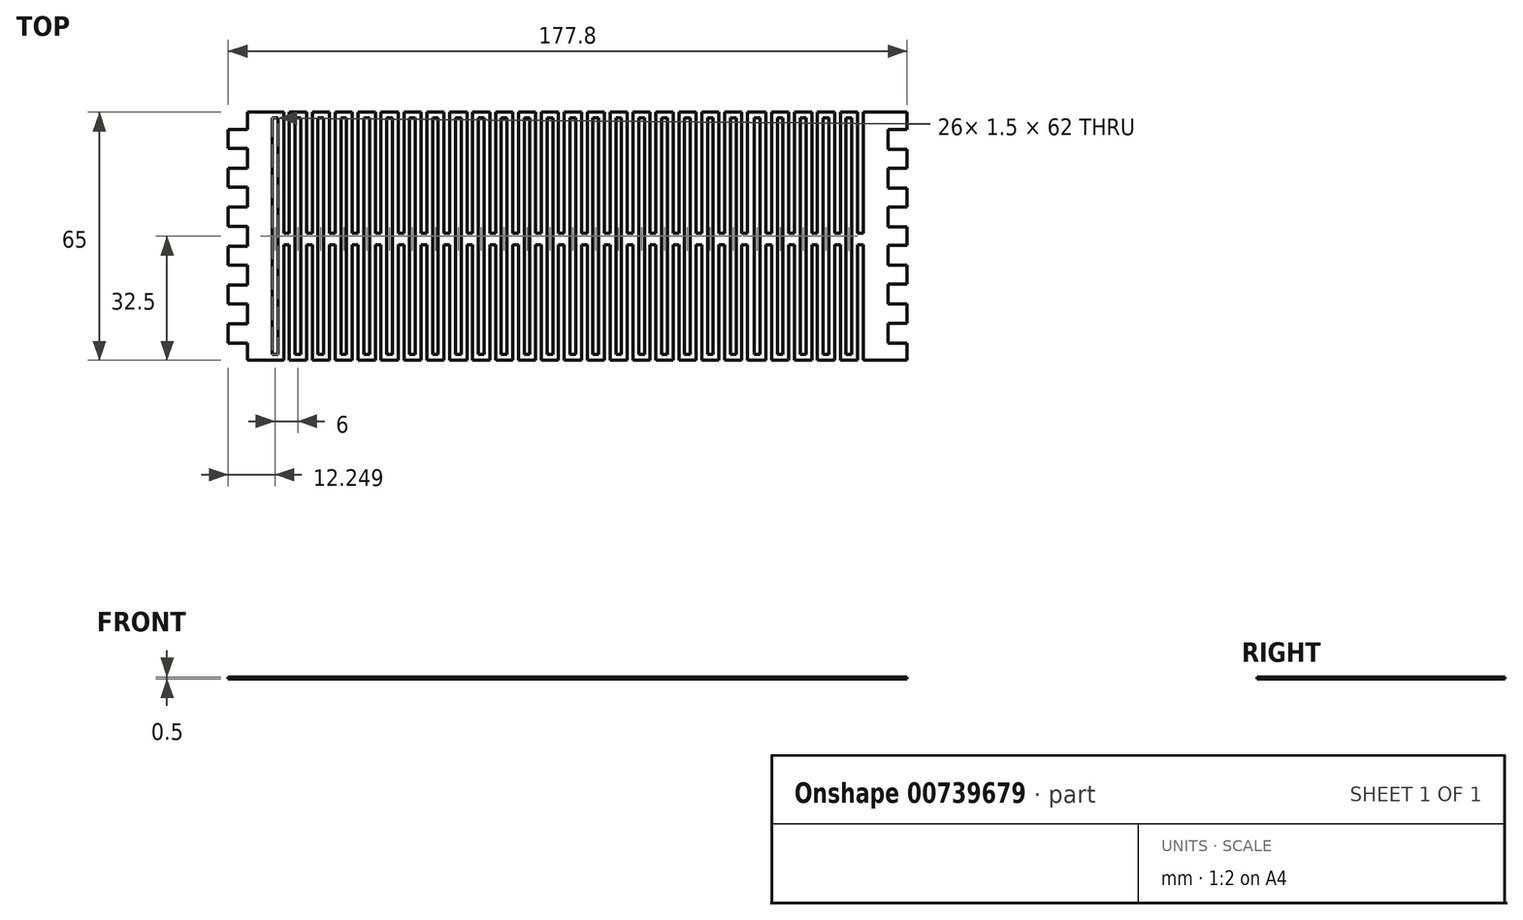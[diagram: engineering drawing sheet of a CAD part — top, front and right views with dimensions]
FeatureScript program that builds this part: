
annotation { "Feature Type Name" : "Feature", "Feature Type Description" : "" }
export const myFeature = defineFeature(function(context is Context, id is Id, definition is map)
    precondition{}
    {
        {
            var Q0;
            Q0=qCreatedBy(makeId("Top.planeOp"),FACE);
            var sketch = newSketch(context, id + "F0", { "sketchPlane" : qUnion([Q0])});
            skLineSegment(sketch, "E0.bottom", {"start": v(-70.46, 0) * mm, "end": v(-60.96, 0) * mm});
            skLineSegment(sketch, "E0.top", {"start": v(-70.46, -65) * mm, "end": v(-65.46, -65) * mm});
            skLineSegment(sketch, "E0.left", {"start": v(-75.46, -4.5) * mm, "end": v(-75.46, -9.5) * mm});
            skLineSegment(sketch, "E0.right", {"start": v(102.34, 0) * mm, "end": v(102.34, -4.5) * mm});
            skLineSegment(sketch, "E1.top", {"start": v(-75.46, -4.5) * mm, "end": v(-70.46, -4.5) * mm});
            skLineSegment(sketch, "E1.right", {"start": v(-70.46, 0) * mm, "end": v(-70.46, -4.5) * mm});
            skLineSegment(sketch, "E2", {"start": v(-70.46, -9.5) * mm, "end": v(-70.46, -14.7) * mm});
            skLineSegment(sketch, "E3", {"start": v(-65.46, 0) * mm, "end": v(-70.46, 0) * mm});
            skLineSegment(sketch, "E4", {"start": v(-75.46, -9.5) * mm, "end": v(-70.46, -9.5) * mm});
            skLineSegment(sketch, "E5", {"start": v(-70.46, -14.7) * mm, "end": v(-75.46, -14.7) * mm});
            skLineSegment(sketch, "E6", {"start": v(-75.46, -14.7) * mm, "end": v(-75.46, -19.7) * mm});
            skLineSegment(sketch, "E7", {"start": v(-75.46, -19.7) * mm, "end": v(-70.46, -19.7) * mm});
            skLineSegment(sketch, "E8", {"start": v(-70.46, -19.7) * mm, "end": v(-70.46, -24.9) * mm});
            skLineSegment(sketch, "E9", {"start": v(-70.46, -24.9) * mm, "end": v(-75.46, -24.9) * mm});
            skLineSegment(sketch, "E10", {"start": v(-75.46, -29.9) * mm, "end": v(-70.46, -29.9) * mm});
            skLineSegment(sketch, "E11", {"start": v(-70.46, -29.9) * mm, "end": v(-70.46, -35.1) * mm});
            skLineSegment(sketch, "E12", {"start": v(-70.46, -35.1) * mm, "end": v(-75.46, -35.1) * mm});
            skLineSegment(sketch, "E13", {"start": v(-75.46, -35.1) * mm, "end": v(-75.46, -40.1) * mm});
            skLineSegment(sketch, "E14", {"start": v(-75.46, -40.1) * mm, "end": v(-70.46, -40.1) * mm});
            skLineSegment(sketch, "E15", {"start": v(-70.46, -40.1) * mm, "end": v(-70.46, -45.3) * mm});
            skLineSegment(sketch, "E16", {"start": v(-70.46, -45.3) * mm, "end": v(-75.46, -45.3) * mm});
            skLineSegment(sketch, "E17", {"start": v(-75.46, -45.3) * mm, "end": v(-75.46, -50.3) * mm});
            skLineSegment(sketch, "E18", {"start": v(-75.46, -50.3) * mm, "end": v(-70.46, -50.3) * mm});
            skLineSegment(sketch, "E19", {"start": v(-70.46, -50.3) * mm, "end": v(-70.46, -55.5) * mm});
            skLineSegment(sketch, "E20", {"start": v(-70.46, -55.5) * mm, "end": v(-75.46, -55.5) * mm});
            skLineSegment(sketch, "E21", {"start": v(-75.46, -55.5) * mm, "end": v(-75.46, -60.5) * mm});
            skLineSegment(sketch, "E22", {"start": v(-75.46, -60.5) * mm, "end": v(-70.46, -60.5) * mm});
            skLineSegment(sketch, "E23", {"start": v(-70.46, -60.5) * mm, "end": v(-70.46, -65) * mm});
            skPoint(sketch, "E24.trimOffspring.end.orphan", {"position": v(-75.46, -65) * mm});
            skPoint(sketch, "E25.orphan", {"position": v(-75.46, 0) * mm});
            skPoint(sketch, "E26.start.orphan", {"position": v(-75.46, -28.38) * mm});
            skLineSegment(sketch, "E27", {"start": v(-75.46, -24.9) * mm, "end": v(-75.46, -29.9) * mm});
            skPoint(sketch, "E28.endSnap0", {"position": v(15.94, -65) * mm});
            skLineSegment(sketch, "E29.MirrorCS", {"start": v(92.34, 0) * mm, "end": v(97.34, 0) * mm});
            skPoint(sketch, "E30.MirrorCS.end.orphan", {"position": v(102.34, -10) * mm});
            skPoint(sketch, "E30.MirrorCS.start.orphan", {"position": v(102.34, -4.5) * mm});
            skPoint(sketch, "E31.MirrorCS.start.orphan", {"position": v(102.34, -34.9) * mm});
            skPoint(sketch, "E32.MirrorCS.end.orphan", {"position": v(102.34, -60.5) * mm});
            skPoint(sketch, "E32.MirrorCS.start.orphan", {"position": v(102.34, -55) * mm});
            skPoint(sketch, "E33.MirrorCS.end.orphan", {"position": v(97.34, -62.94) * mm});
            skPoint(sketch, "E34.MirrorCS.start.orphan", {"position": v(97.34, -50) * mm});
            skPoint(sketch, "E35.MirrorCS.start.orphan", {"position": v(97.34, -40.1) * mm});
            skPoint(sketch, "E36.MirrorCS.start.orphan", {"position": v(97.34, -30) * mm});
            skPoint(sketch, "E37.MirrorCS.end.orphan", {"position": v(97.34, -25) * mm});
            skPoint(sketch, "E37.MirrorCS.start.orphan", {"position": v(97.34, -20) * mm});
            skPoint(sketch, "E38.MirrorCS.start.orphan", {"position": v(97.34, -10) * mm});
            skPoint(sketch, "E39.MirrorCS.start.orphan", {"position": v(97.34, 0) * mm});
            skPoint(sketch, "E28.end.orphan", {"position": v(13.44, -65) * mm});
            skLineSegment(sketch, "E40", {"start": v(13.44, -65) * mm, "end": v(15.94, -65) * mm});
            skLineSegment(sketch, "E41", {"start": v(13.44, -65) * mm, "end": v(12.54, -65) * mm});
            skLineSegment(sketch, "E42", {"start": v(-70.46, -65) * mm, "end": v(-70.46, -60.5) * mm});
            skLineSegment(sketch, "E43", {"start": v(-70.46, -4.5) * mm, "end": v(-70.46, 0) * mm});
            skLineSegment(sketch, "E44", {"start": v(102.34, -9.7) * mm, "end": v(102.34, -14.7) * mm});
            skLineSegment(sketch, "E45", {"start": v(102.34, -65) * mm, "end": v(102.34, -60.5) * mm});
            skLineSegment(sketch, "E46", {"start": v(97.34, -4.5) * mm, "end": v(97.34, -9.7) * mm});
            skLineSegment(sketch, "E47", {"start": v(102.34, -60.5) * mm, "end": v(97.34, -60.5) * mm});
            skLineSegment(sketch, "E48", {"start": v(97.34, -60.5) * mm, "end": v(97.34, -55.3) * mm});
            skLineSegment(sketch, "E49", {"start": v(97.34, -55.3) * mm, "end": v(102.34, -55.3) * mm});
            skLineSegment(sketch, "E50", {"start": v(102.34, -55.3) * mm, "end": v(102.34, -50.3) * mm});
            skLineSegment(sketch, "E51", {"start": v(102.34, -50.3) * mm, "end": v(97.34, -50.3) * mm});
            skLineSegment(sketch, "E52", {"start": v(97.34, -50.3) * mm, "end": v(97.34, -45.1) * mm});
            skLineSegment(sketch, "E53", {"start": v(97.34, -45.1) * mm, "end": v(102.34, -45.1) * mm});
            skLineSegment(sketch, "E54", {"start": v(102.34, -45.1) * mm, "end": v(102.34, -40.1) * mm});
            skLineSegment(sketch, "E55", {"start": v(102.34, -40.1) * mm, "end": v(97.34, -40.1) * mm});
            skLineSegment(sketch, "E56", {"start": v(97.34, -40.1) * mm, "end": v(97.34, -34.9) * mm});
            skLineSegment(sketch, "E57.trimOffspring", {"start": v(102.34, -60.5) * mm, "end": v(102.34, -65) * mm});
            skLineSegment(sketch, "E58.trimOffspring", {"start": v(102.34, -50.3) * mm, "end": v(102.34, -55.3) * mm});
            skLineSegment(sketch, "E59.trimOffspring", {"start": v(102.34, -40.1) * mm, "end": v(102.34, -45.1) * mm});
            skLineSegment(sketch, "E60.trimOffspring", {"start": v(97.34, -55.3) * mm, "end": v(97.34, -60.5) * mm});
            skLineSegment(sketch, "E61.trimOffspring", {"start": v(97.34, -45.1) * mm, "end": v(97.34, -50.3) * mm});
            skLineSegment(sketch, "E62", {"start": v(102.34, -34.9) * mm, "end": v(97.34, -34.9) * mm});
            skLineSegment(sketch, "E63", {"start": v(97.34, -30.1) * mm, "end": v(102.34, -30.1) * mm});
            skLineSegment(sketch, "E64", {"start": v(102.34, -30.1) * mm, "end": v(102.34, -34.9) * mm});
            skLineSegment(sketch, "E65", {"start": v(97.34, -34.9) * mm, "end": v(97.34, -40.1) * mm});
            skLineSegment(sketch, "E66", {"start": v(97.34, -30.1) * mm, "end": v(97.34, -24.9) * mm});
            skLineSegment(sketch, "E67", {"start": v(97.34, -24.9) * mm, "end": v(102.34, -24.9) * mm});
            skLineSegment(sketch, "E68", {"start": v(102.34, -24.9) * mm, "end": v(102.34, -19.9) * mm});
            skLineSegment(sketch, "E69", {"start": v(102.34, -19.9) * mm, "end": v(97.34, -19.9) * mm});
            skLineSegment(sketch, "E70", {"start": v(97.34, -19.9) * mm, "end": v(97.34, -14.7) * mm});
            skLineSegment(sketch, "E71", {"start": v(97.34, -14.7) * mm, "end": v(102.34, -14.7) * mm});
            skLineSegment(sketch, "E72.trimOffspring", {"start": v(102.34, -19.9) * mm, "end": v(102.34, -24.9) * mm});
            skLineSegment(sketch, "E73.trimOffspring", {"start": v(97.34, -24.9) * mm, "end": v(97.34, -30.1) * mm});
            skLineSegment(sketch, "E74", {"start": v(97.34, -19.9) * mm, "end": v(102.34, -19.9) * mm});
            skLineSegment(sketch, "E75", {"start": v(102.34, -14.7) * mm, "end": v(102.34, -9.7) * mm});
            skLineSegment(sketch, "E76", {"start": v(102.34, -9.7) * mm, "end": v(97.34, -9.7) * mm});
            skLineSegment(sketch, "E77", {"start": v(97.34, -9.7) * mm, "end": v(97.34, -4.5) * mm});
            skLineSegment(sketch, "E78", {"start": v(97.34, -4.5) * mm, "end": v(102.34, -4.5) * mm});
            skLineSegment(sketch, "E79.trimOffspring", {"start": v(97.34, -14.7) * mm, "end": v(97.34, -19.9) * mm});
            skLineSegment(sketch, "E80.trimOffspring", {"start": v(13.44, -65) * mm, "end": v(17.04, -65) * mm});
            skLineSegment(sketch, "E81.bottom", {"start": v(-65.46, -65) * mm, "end": v(-63.96, -65) * mm});
            skLineSegment(sketch, "E82.bottom", {"start": v(-65.46, 0) * mm, "end": v(-63.96, 0) * mm});
            skLineSegment(sketch, "E83.bottom", {"start": v(-63.96, -1.5) * mm, "end": v(-62.46, -1.5) * mm});
            skLineSegment(sketch, "E83.top", {"start": v(-63.96, -63.5) * mm, "end": v(-62.46, -63.5) * mm});
            skLineSegment(sketch, "E83.left", {"start": v(-63.96, -1.5) * mm, "end": v(-63.96, -63.5) * mm});
            skLineSegment(sketch, "E83.right", {"start": v(-62.46, -1.5) * mm, "end": v(-62.46, -63.5) * mm});
            skPoint(sketch, "E81.top.end.orphan", {"position": v(-63.96, -63.5) * mm});
            skLineSegment(sketch, "E84.top", {"start": v(-62.46, -65) * mm, "end": v(-60.96, -65) * mm});
            skLineSegment(sketch, "E85.left", {"start": v(-60.96, -65) * mm, "end": v(-60.96, -34.75) * mm});
            skLineSegment(sketch, "E85.right", {"start": v(-59.46, -65) * mm, "end": v(-59.46, -34.75) * mm});
            skLineSegment(sketch, "E86.trimOffspring", {"start": v(-60.96, -65) * mm, "end": v(-70.46, -65) * mm});
            skLineSegment(sketch, "E87.top", {"start": v(-62.46, 0) * mm, "end": v(-60.96, 0) * mm});
            skLineSegment(sketch, "E87.right", {"start": v(-60.96, -1.5) * mm, "end": v(-60.96, 0) * mm});
            skLineSegment(sketch, "E88.top", {"start": v(-60.96, -31.75) * mm, "end": v(-59.46, -31.75) * mm});
            skLineSegment(sketch, "E88.left", {"start": v(-60.96, -1.5) * mm, "end": v(-60.96, -31.75) * mm});
            skLineSegment(sketch, "E88.right", {"start": v(-59.46, -1.5) * mm, "end": v(-59.46, -31.75) * mm});
            skLineSegment(sketch, "E89.trimOffspring", {"start": v(13.44, 0) * mm, "end": v(17.04, 0) * mm});
            skLineSegment(sketch, "E90", {"start": v(-59.46, -1.5) * mm, "end": v(-59.46, 0) * mm});
            skLineSegment(sketch, "E91.trimOffspring", {"start": v(-59.46, 0) * mm, "end": v(-54.96, 0) * mm});
            skLineSegment(sketch, "E92.bottom", {"start": v(-59.46, -65) * mm, "end": v(-57.96, -65) * mm});
            skLineSegment(sketch, "E92.left", {"start": v(-59.46, -65) * mm, "end": v(-59.46, -63.5) * mm});
            skLineSegment(sketch, "E93.bottom", {"start": v(-59.46, 0) * mm, "end": v(-57.96, 0) * mm});
            skLineSegment(sketch, "E93.left", {"start": v(-59.46, 0) * mm, "end": v(-59.46, -1.5) * mm});
            skLineSegment(sketch, "E94.bottom", {"start": v(-57.96, -1.5) * mm, "end": v(-56.46, -1.5) * mm});
            skLineSegment(sketch, "E94.top", {"start": v(-57.96, -63.5) * mm, "end": v(-56.46, -63.5) * mm});
            skLineSegment(sketch, "E94.left", {"start": v(-57.96, -1.5) * mm, "end": v(-57.96, -63.5) * mm});
            skLineSegment(sketch, "E94.right", {"start": v(-56.46, -1.5) * mm, "end": v(-56.46, -63.5) * mm});
            skLineSegment(sketch, "E95.trimOffspring", {"start": v(-59.46, -31.75) * mm, "end": v(-60.96, -31.75) * mm});
            skLineSegment(sketch, "E96.top", {"start": v(-56.46, -65) * mm, "end": v(-54.96, -65) * mm});
            skLineSegment(sketch, "E97.bottom", {"start": v(-56.46, -1.5) * mm, "end": v(-54.96, -1.5) * mm});
            skLineSegment(sketch, "E97.top", {"start": v(-56.46, 0) * mm, "end": v(-54.96, 0) * mm});
            skLineSegment(sketch, "E98.top", {"start": v(-54.96, -31.75) * mm, "end": v(-53.46, -31.75) * mm});
            skLineSegment(sketch, "E98.left", {"start": v(-54.96, -1.5) * mm, "end": v(-54.96, -31.75) * mm});
            skLineSegment(sketch, "E98.right", {"start": v(-53.46, -1.5) * mm, "end": v(-53.46, -31.75) * mm});
            skLineSegment(sketch, "E99", {"start": v(-54.96, -1.5) * mm, "end": v(-54.96, 0) * mm});
            skLineSegment(sketch, "E100", {"start": v(-53.46, -1.5) * mm, "end": v(-53.46, 0) * mm});
            skLineSegment(sketch, "E101.trimOffspring", {"start": v(-53.46, 0) * mm, "end": v(-48.96, 0) * mm});
            skPoint(sketch, "E96.right.start.orphan", {"position": v(-54.96, -63.5) * mm});
            skLineSegment(sketch, "E102.left", {"start": v(-54.96, -65) * mm, "end": v(-54.96, -34.75) * mm});
            skLineSegment(sketch, "E102.right", {"start": v(-53.46, -65) * mm, "end": v(-53.46, -34.75) * mm});
            skLineSegment(sketch, "E103.trimOffspring", {"start": v(-54.96, -65) * mm, "end": v(-59.46, -65) * mm});
            skLineSegment(sketch, "E104.bottom", {"start": v(-53.46, -65) * mm, "end": v(-51.96, -65) * mm});
            skLineSegment(sketch, "E104.left", {"start": v(-53.46, -65) * mm, "end": v(-53.46, -63.5) * mm});
            skLineSegment(sketch, "E105.bottom", {"start": v(-53.46, 0) * mm, "end": v(-51.96, 0) * mm});
            skLineSegment(sketch, "E105.left", {"start": v(-53.46, 0) * mm, "end": v(-53.46, -1.5) * mm});
            skLineSegment(sketch, "E106.bottom", {"start": v(-51.96, -1.5) * mm, "end": v(-50.46, -1.5) * mm});
            skLineSegment(sketch, "E106.top", {"start": v(-51.96, -63.5) * mm, "end": v(-50.46, -63.5) * mm});
            skLineSegment(sketch, "E106.left", {"start": v(-51.96, -1.5) * mm, "end": v(-51.96, -63.5) * mm});
            skLineSegment(sketch, "E106.right", {"start": v(-50.46, -1.5) * mm, "end": v(-50.46, -63.5) * mm});
            skLineSegment(sketch, "E107.trimOffspring", {"start": v(-53.46, -31.75) * mm, "end": v(-54.96, -31.75) * mm});
            skLineSegment(sketch, "E108.top", {"start": v(-50.46, -65) * mm, "end": v(-48.96, -65) * mm});
            skLineSegment(sketch, "E108.right", {"start": v(-48.96, -63.5) * mm, "end": v(-48.96, -65) * mm});
            skLineSegment(sketch, "E109.left", {"start": v(-48.96, -65) * mm, "end": v(-48.96, -34.75) * mm});
            skLineSegment(sketch, "E109.right", {"start": v(-47.46, -65) * mm, "end": v(-47.46, -34.75) * mm});
            skLineSegment(sketch, "E110.trimOffspring", {"start": v(-48.96, -65) * mm, "end": v(-53.46, -65) * mm});
            skLineSegment(sketch, "E111.top", {"start": v(-50.46, 0) * mm, "end": v(-48.96, 0) * mm});
            skLineSegment(sketch, "E111.right", {"start": v(-48.96, -1.5) * mm, "end": v(-48.96, 0) * mm});
            skLineSegment(sketch, "E112.top", {"start": v(-48.96, -31.75) * mm, "end": v(-47.46, -31.75) * mm});
            skLineSegment(sketch, "E112.left", {"start": v(-48.96, -1.5) * mm, "end": v(-48.96, -31.75) * mm});
            skLineSegment(sketch, "E112.right", {"start": v(-47.46, -1.5) * mm, "end": v(-47.46, -31.75) * mm});
            skLineSegment(sketch, "E113", {"start": v(-47.46, -1.5) * mm, "end": v(-47.46, 0) * mm});
            skLineSegment(sketch, "E114.trimOffspring", {"start": v(-47.46, 0) * mm, "end": v(-42.96, 0) * mm});
            skLineSegment(sketch, "E115.bottom", {"start": v(-47.46, -65) * mm, "end": v(-45.96, -65) * mm});
            skLineSegment(sketch, "E115.left", {"start": v(-47.46, -65) * mm, "end": v(-47.46, -63.5) * mm});
            skLineSegment(sketch, "E116.bottom", {"start": v(-47.46, 0) * mm, "end": v(-45.96, 0) * mm});
            skLineSegment(sketch, "E116.left", {"start": v(-47.46, 0) * mm, "end": v(-47.46, -1.5) * mm});
            skLineSegment(sketch, "E117.bottom", {"start": v(-45.96, -1.5) * mm, "end": v(-44.46, -1.5) * mm});
            skLineSegment(sketch, "E117.top", {"start": v(-45.96, -63.5) * mm, "end": v(-44.46, -63.5) * mm});
            skLineSegment(sketch, "E117.left", {"start": v(-45.96, -1.5) * mm, "end": v(-45.96, -63.5) * mm});
            skLineSegment(sketch, "E117.right", {"start": v(-44.46, -1.5) * mm, "end": v(-44.46, -63.5) * mm});
            skLineSegment(sketch, "E118.trimOffspring", {"start": v(-47.46, -31.75) * mm, "end": v(-48.96, -31.75) * mm});
            skLineSegment(sketch, "E119.top", {"start": v(-44.46, -65) * mm, "end": v(-42.96, -65) * mm});
            skLineSegment(sketch, "E119.right", {"start": v(-42.96, -63.5) * mm, "end": v(-42.96, -65) * mm});
            skLineSegment(sketch, "E120.left", {"start": v(-42.96, -65) * mm, "end": v(-42.96, -34.75) * mm});
            skLineSegment(sketch, "E120.right", {"start": v(-41.46, -65) * mm, "end": v(-41.46, -34.75) * mm});
            skLineSegment(sketch, "E121.trimOffspring", {"start": v(-42.96, -65) * mm, "end": v(-47.46, -65) * mm});
            skLineSegment(sketch, "E122.top", {"start": v(-44.46, 0) * mm, "end": v(-42.96, 0) * mm});
            skLineSegment(sketch, "E122.right", {"start": v(-42.96, -1.5) * mm, "end": v(-42.96, 0) * mm});
            skLineSegment(sketch, "E123.top", {"start": v(-42.96, -31.75) * mm, "end": v(-41.46, -31.75) * mm});
            skLineSegment(sketch, "E123.left", {"start": v(-42.96, 0) * mm, "end": v(-42.96, -31.75) * mm});
            skLineSegment(sketch, "E123.right", {"start": v(-41.46, 0) * mm, "end": v(-41.46, -31.75) * mm});
            skLineSegment(sketch, "E124.trimOffspring", {"start": v(-41.46, 0) * mm, "end": v(-36.96, 0) * mm});
            skLineSegment(sketch, "E125.bottom", {"start": v(-41.46, -65) * mm, "end": v(-39.96, -65) * mm});
            skLineSegment(sketch, "E125.left", {"start": v(-41.46, -65) * mm, "end": v(-41.46, -63.5) * mm});
            skLineSegment(sketch, "E126.bottom", {"start": v(-41.46, 0) * mm, "end": v(-39.96, 0) * mm});
            skLineSegment(sketch, "E126.left", {"start": v(-41.46, 0) * mm, "end": v(-41.46, -1.5) * mm});
            skLineSegment(sketch, "E127.bottom", {"start": v(-39.96, -1.5) * mm, "end": v(-38.46, -1.5) * mm});
            skLineSegment(sketch, "E127.top", {"start": v(-39.96, -63.5) * mm, "end": v(-38.46, -63.5) * mm});
            skLineSegment(sketch, "E127.left", {"start": v(-39.96, -1.5) * mm, "end": v(-39.96, -63.5) * mm});
            skLineSegment(sketch, "E127.right", {"start": v(-38.46, -1.5) * mm, "end": v(-38.46, -63.5) * mm});
            skPoint(sketch, "E125.right.end.orphan", {"position": v(-39.96, -63.5) * mm});
            skLineSegment(sketch, "E128.trimOffspring", {"start": v(-41.46, -31.75) * mm, "end": v(-42.96, -31.75) * mm});
            skLineSegment(sketch, "E129.top", {"start": v(-38.46, -65) * mm, "end": v(-36.96, -65) * mm});
            skLineSegment(sketch, "E130.top", {"start": v(-38.46, 0) * mm, "end": v(-36.96, 0) * mm});
            skLineSegment(sketch, "E130.right", {"start": v(-36.96, -1.5) * mm, "end": v(-36.96, 0) * mm});
            skLineSegment(sketch, "E131.top", {"start": v(-36.96, -31.75) * mm, "end": v(-35.46, -31.75) * mm});
            skLineSegment(sketch, "E131.left", {"start": v(-36.96, -1.5) * mm, "end": v(-36.96, -31.75) * mm});
            skLineSegment(sketch, "E131.right", {"start": v(-35.46, -1.5) * mm, "end": v(-35.46, -31.75) * mm});
            skLineSegment(sketch, "E132", {"start": v(-35.46, -1.5) * mm, "end": v(-35.46, 0) * mm});
            skLineSegment(sketch, "E133.trimOffspring", {"start": v(-35.46, 0) * mm, "end": v(-32.46, 0) * mm});
            skLineSegment(sketch, "E134.right", {"start": v(-36.96, -65) * mm, "end": v(-36.96, -63.5) * mm});
            skLineSegment(sketch, "E135.top", {"start": v(-36.96, -34.75) * mm, "end": v(-35.46, -34.75) * mm});
            skLineSegment(sketch, "E135.left", {"start": v(-36.96, -65) * mm, "end": v(-36.96, -34.75) * mm});
            skLineSegment(sketch, "E135.right", {"start": v(-35.46, -65) * mm, "end": v(-35.46, -34.75) * mm});
            skLineSegment(sketch, "E136.trimOffspring", {"start": v(-38.46, -65) * mm, "end": v(-41.46, -65) * mm});
            skLineSegment(sketch, "E137.bottom", {"start": v(-35.46, -65) * mm, "end": v(-33.96, -65) * mm});
            skLineSegment(sketch, "E137.left", {"start": v(-35.46, -65) * mm, "end": v(-35.46, -63.5) * mm});
            skLineSegment(sketch, "E138.bottom", {"start": v(-35.46, 0) * mm, "end": v(-33.96, 0) * mm});
            skLineSegment(sketch, "E138.left", {"start": v(-35.46, 0) * mm, "end": v(-35.46, -1.5) * mm});
            skLineSegment(sketch, "E139.bottom", {"start": v(-33.96, -1.5) * mm, "end": v(-32.46, -1.5) * mm});
            skLineSegment(sketch, "E139.top", {"start": v(-33.96, -63.5) * mm, "end": v(-32.46, -63.5) * mm});
            skLineSegment(sketch, "E139.left", {"start": v(-33.96, -1.5) * mm, "end": v(-33.96, -63.5) * mm});
            skLineSegment(sketch, "E139.right", {"start": v(-32.46, -1.5) * mm, "end": v(-32.46, -63.5) * mm});
            skPoint(sketch, "E137.top.end.orphan", {"position": v(-33.96, -63.5) * mm});
            skLineSegment(sketch, "E140.trimOffspring", {"start": v(-35.46, -31.75) * mm, "end": v(-36.96, -31.75) * mm});
            skLineSegment(sketch, "E141.trimOffspring", {"start": v(-59.46, -34.75) * mm, "end": v(-60.96, -34.75) * mm});
            skLineSegment(sketch, "E142.trimOffspring", {"start": v(-53.46, -34.75) * mm, "end": v(-54.96, -34.75) * mm});
            skLineSegment(sketch, "E143.trimOffspring", {"start": v(-47.46, -34.75) * mm, "end": v(-48.96, -34.75) * mm});
            skLineSegment(sketch, "E144.trimOffspring", {"start": v(-41.46, -34.75) * mm, "end": v(-42.96, -34.75) * mm});
            skLineSegment(sketch, "E145.trimOffspring", {"start": v(-35.46, -34.75) * mm, "end": v(-36.96, -34.75) * mm});
            skLineSegment(sketch, "E146.MirrorCS", {"start": v(62.34, -1.5) * mm, "end": v(62.34, -31.75) * mm});
            skLineSegment(sketch, "E147.MirrorCS", {"start": v(63.84, -1.5) * mm, "end": v(63.84, -31.75) * mm});
            skLineSegment(sketch, "E148.MirrorCS", {"start": v(65.34, -1.5) * mm, "end": v(65.34, -31.75) * mm});
            skLineSegment(sketch, "E149.MirrorCS", {"start": v(68.34, -1.5) * mm, "end": v(68.34, -31.75) * mm});
            skLineSegment(sketch, "E150.MirrorCS", {"start": v(69.84, -1.5) * mm, "end": v(69.84, -31.75) * mm});
            skLineSegment(sketch, "E151.MirrorCS", {"start": v(90.84, -1.5) * mm, "end": v(90.84, -31.75) * mm});
            skLineSegment(sketch, "E152.MirrorCS", {"start": v(89.34, -1.5) * mm, "end": v(89.34, -31.75) * mm});
            skLineSegment(sketch, "E153.MirrorCS", {"start": v(87.84, -1.5) * mm, "end": v(87.84, -31.75) * mm});
            skLineSegment(sketch, "E154.MirrorCS", {"start": v(86.34, -1.5) * mm, "end": v(86.34, -31.75) * mm});
            skLineSegment(sketch, "E155.MirrorCS", {"start": v(84.84, -1.5) * mm, "end": v(84.84, -31.75) * mm});
            skLineSegment(sketch, "E156.MirrorCS", {"start": v(81.84, -1.5) * mm, "end": v(81.84, -31.75) * mm});
            skLineSegment(sketch, "E157.MirrorCS", {"start": v(80.34, -1.5) * mm, "end": v(80.34, -31.75) * mm});
            skLineSegment(sketch, "E158.MirrorCS", {"start": v(78.84, -1.5) * mm, "end": v(78.84, -31.75) * mm});
            skLineSegment(sketch, "E159.MirrorCS", {"start": v(77.34, -1.5) * mm, "end": v(77.34, -31.75) * mm});
            skLineSegment(sketch, "E160.MirrorCS", {"start": v(75.84, -1.5) * mm, "end": v(75.84, -31.75) * mm});
            skLineSegment(sketch, "E161.MirrorCS", {"start": v(74.34, -1.5) * mm, "end": v(74.34, -31.75) * mm});
            skLineSegment(sketch, "E162.MirrorCS", {"start": v(72.84, -1.5) * mm, "end": v(72.84, -31.75) * mm});
            skLineSegment(sketch, "E163.MirrorCS", {"start": v(71.34, -1.5) * mm, "end": v(71.34, -31.75) * mm});
            skLineSegment(sketch, "E164.MirrorCS", {"start": v(62.34, -63.5) * mm, "end": v(62.34, -34.75) * mm});
            skLineSegment(sketch, "E165.MirrorCS", {"start": v(63.84, -63.5) * mm, "end": v(63.84, -34.75) * mm});
            skLineSegment(sketch, "E166.MirrorCS", {"start": v(68.34, -63.5) * mm, "end": v(68.34, -34.75) * mm});
            skLineSegment(sketch, "E167.MirrorCS", {"start": v(69.84, -63.5) * mm, "end": v(69.84, -34.75) * mm});
            skLineSegment(sketch, "E168.MirrorCS", {"start": v(75.84, -63.5) * mm, "end": v(75.84, -34.75) * mm});
            skLineSegment(sketch, "E169.MirrorCS", {"start": v(80.34, -63.5) * mm, "end": v(80.34, -34.75) * mm});
            skLineSegment(sketch, "E170.MirrorCS", {"start": v(81.84, -63.5) * mm, "end": v(81.84, -34.75) * mm});
            skLineSegment(sketch, "E171.MirrorCS", {"start": v(87.84, -63.5) * mm, "end": v(87.84, -34.75) * mm});
            skLineSegment(sketch, "E172.MirrorCS", {"start": v(66.84, -1.5) * mm, "end": v(66.84, -31.75) * mm});
            skLineSegment(sketch, "E173.MirrorCS", {"start": v(74.34, -63.5) * mm, "end": v(74.34, -34.75) * mm});
            skLineSegment(sketch, "E174.MirrorCS", {"start": v(86.34, -63.5) * mm, "end": v(86.34, -34.75) * mm});
            skLineSegment(sketch, "E175.MirrorCS", {"start": v(83.34, -1.5) * mm, "end": v(83.34, -31.75) * mm});
            skLineSegment(sketch, "E176.trimOffspring", {"start": v(63.84, -65) * mm, "end": v(65.34, -65) * mm});
            skLineSegment(sketch, "E177.trimOffspring", {"start": v(69.84, -65) * mm, "end": v(71.34, -65) * mm});
            skLineSegment(sketch, "E178.trimOffspring", {"start": v(75.84, -65) * mm, "end": v(77.34, -65) * mm});
            skLineSegment(sketch, "E179.trimOffspring", {"start": v(81.84, -65) * mm, "end": v(83.34, -65) * mm});
            skLineSegment(sketch, "E180.trimOffspring", {"start": v(87.84, -65) * mm, "end": v(89.34, -65) * mm});
            skLineSegment(sketch, "E181.trimOffspring", {"start": v(63.84, 0) * mm, "end": v(65.34, 0) * mm});
            skLineSegment(sketch, "E182.trimOffspring", {"start": v(69.84, 0) * mm, "end": v(71.34, 0) * mm});
            skLineSegment(sketch, "E183.trimOffspring", {"start": v(81.84, 0) * mm, "end": v(83.34, 0) * mm});
            skLineSegment(sketch, "E184.trimOffspring", {"start": v(87.84, 0) * mm, "end": v(89.34, 0) * mm});
            skLineSegment(sketch, "E185.trimOffspring", {"start": v(-36.96, -65) * mm, "end": v(-41.46, -65) * mm});
            skLineSegment(sketch, "E186.trimOffspring", {"start": v(-42.96, -65) * mm, "end": v(-45.96, -65) * mm});
            skLineSegment(sketch, "E187.trimOffspring", {"start": v(-48.96, -65) * mm, "end": v(-51.96, -65) * mm});
            skLineSegment(sketch, "E188.trimOffspring", {"start": v(-60.96, -65) * mm, "end": v(-75.46, -65) * mm});
            skLineSegment(sketch, "E189.top", {"start": v(-32.46, -65) * mm, "end": v(-30.96, -65) * mm});
            skLineSegment(sketch, "E189.right", {"start": v(-30.96, -63.5) * mm, "end": v(-30.96, -65) * mm});
            skLineSegment(sketch, "E190.top", {"start": v(-32.46, 0) * mm, "end": v(-30.96, 0) * mm});
            skLineSegment(sketch, "E190.right", {"start": v(-30.96, -1.5) * mm, "end": v(-30.96, 0) * mm});
            skLineSegment(sketch, "E191.top", {"start": v(-30.96, -34.75) * mm, "end": v(-29.46, -34.75) * mm});
            skLineSegment(sketch, "E191.left", {"start": v(-30.96, -63.5) * mm, "end": v(-30.96, -34.75) * mm});
            skLineSegment(sketch, "E191.right", {"start": v(-29.46, -63.5) * mm, "end": v(-29.46, -34.75) * mm});
            skLineSegment(sketch, "E192.top", {"start": v(-30.96, -31.75) * mm, "end": v(-29.46, -31.75) * mm});
            skLineSegment(sketch, "E192.left", {"start": v(-30.96, -1.5) * mm, "end": v(-30.96, -31.75) * mm});
            skLineSegment(sketch, "E192.right", {"start": v(-29.46, -1.5) * mm, "end": v(-29.46, -31.75) * mm});
            skLineSegment(sketch, "E193", {"start": v(-29.46, -63.5) * mm, "end": v(-29.46, -65) * mm});
            skLineSegment(sketch, "E194", {"start": v(-29.46, -65) * mm, "end": v(-29.46, -34.75) * mm});
            skLineSegment(sketch, "E195", {"start": v(-29.46, -1.5) * mm, "end": v(-29.46, 0) * mm});
            skLineSegment(sketch, "E196.trimOffspring", {"start": v(-29.46, 0) * mm, "end": v(-26.46, 0) * mm});
            skLineSegment(sketch, "E197.trimOffspring", {"start": v(-30.96, -65) * mm, "end": v(-35.46, -65) * mm});
            skLineSegment(sketch, "E198.trimOffspring", {"start": v(-30.96, -65) * mm, "end": v(-33.96, -65) * mm});
            skLineSegment(sketch, "E199.trimOffspring", {"start": v(-29.46, -31.75) * mm, "end": v(-29.46, -1.5) * mm});
            skLineSegment(sketch, "E200.bottom", {"start": v(-29.46, -65) * mm, "end": v(-27.96, -65) * mm});
            skLineSegment(sketch, "E200.left", {"start": v(-29.46, -65) * mm, "end": v(-29.46, -63.5) * mm});
            skLineSegment(sketch, "E201.bottom", {"start": v(-29.46, 0) * mm, "end": v(-27.96, 0) * mm});
            skLineSegment(sketch, "E201.left", {"start": v(-29.46, 0) * mm, "end": v(-29.46, -1.5) * mm});
            skLineSegment(sketch, "E202.bottom", {"start": v(-27.96, -1.5) * mm, "end": v(-26.46, -1.5) * mm});
            skLineSegment(sketch, "E202.top", {"start": v(-27.96, -63.5) * mm, "end": v(-26.46, -63.5) * mm});
            skLineSegment(sketch, "E202.left", {"start": v(-27.96, -1.5) * mm, "end": v(-27.96, -63.5) * mm});
            skLineSegment(sketch, "E202.right", {"start": v(-26.46, -1.5) * mm, "end": v(-26.46, -63.5) * mm});
            skLineSegment(sketch, "E203.trimOffspring", {"start": v(-29.46, -34.75) * mm, "end": v(-30.96, -34.75) * mm});
            skLineSegment(sketch, "E204.trimOffspring", {"start": v(-29.46, -31.75) * mm, "end": v(-30.96, -31.75) * mm});
            skLineSegment(sketch, "E205.top", {"start": v(-26.46, -65) * mm, "end": v(-24.96, -65) * mm});
            skLineSegment(sketch, "E205.right", {"start": v(-24.96, -63.5) * mm, "end": v(-24.96, -65) * mm});
            skLineSegment(sketch, "E206.top", {"start": v(-26.46, 0) * mm, "end": v(-24.96, 0) * mm});
            skLineSegment(sketch, "E206.right", {"start": v(-24.96, -1.5) * mm, "end": v(-24.96, 0) * mm});
            skLineSegment(sketch, "E207.top", {"start": v(-24.96, -31.75) * mm, "end": v(-23.46, -31.75) * mm});
            skLineSegment(sketch, "E207.left", {"start": v(-24.96, 0) * mm, "end": v(-24.96, -31.75) * mm});
            skLineSegment(sketch, "E207.right", {"start": v(-23.46, 0) * mm, "end": v(-23.46, -31.75) * mm});
            skLineSegment(sketch, "E208.top", {"start": v(-24.96, -34.75) * mm, "end": v(-23.46, -34.75) * mm});
            skLineSegment(sketch, "E208.left", {"start": v(-24.96, -65) * mm, "end": v(-24.96, -34.75) * mm});
            skLineSegment(sketch, "E208.right", {"start": v(-23.46, -65) * mm, "end": v(-23.46, -34.75) * mm});
            skLineSegment(sketch, "E209.trimOffspring", {"start": v(-24.96, -65) * mm, "end": v(-29.46, -65) * mm});
            skLineSegment(sketch, "E210.trimOffspring", {"start": v(-23.46, 0) * mm, "end": v(-18.96, 0) * mm});
            skLineSegment(sketch, "E211.bottom", {"start": v(-23.46, -65) * mm, "end": v(-21.96, -65) * mm});
            skLineSegment(sketch, "E211.left", {"start": v(-23.46, -65) * mm, "end": v(-23.46, -63.5) * mm});
            skLineSegment(sketch, "E212.bottom", {"start": v(-23.46, 0) * mm, "end": v(-21.96, 0) * mm});
            skLineSegment(sketch, "E212.left", {"start": v(-23.46, 0) * mm, "end": v(-23.46, -1.5) * mm});
            skLineSegment(sketch, "E213.bottom", {"start": v(-21.96, -1.5) * mm, "end": v(-20.46, -1.5) * mm});
            skLineSegment(sketch, "E213.top", {"start": v(-21.96, -63.5) * mm, "end": v(-20.46, -63.5) * mm});
            skLineSegment(sketch, "E213.left", {"start": v(-21.96, -1.5) * mm, "end": v(-21.96, -63.5) * mm});
            skLineSegment(sketch, "E213.right", {"start": v(-20.46, -1.5) * mm, "end": v(-20.46, -63.5) * mm});
            skPoint(sketch, "E211.right.end.orphan", {"position": v(-21.96, -63.5) * mm});
            skLineSegment(sketch, "E214.top", {"start": v(-20.46, -65) * mm, "end": v(-18.96, -65) * mm});
            skLineSegment(sketch, "E214.right", {"start": v(-18.96, -63.5) * mm, "end": v(-18.96, -65) * mm});
            skLineSegment(sketch, "E215.top", {"start": v(-20.46, 0) * mm, "end": v(-18.96, 0) * mm});
            skLineSegment(sketch, "E215.right", {"start": v(-18.96, -1.5) * mm, "end": v(-18.96, 0) * mm});
            skLineSegment(sketch, "E216.top", {"start": v(-18.96, -31.75) * mm, "end": v(-17.46, -31.75) * mm});
            skLineSegment(sketch, "E216.left", {"start": v(-18.96, 0) * mm, "end": v(-18.96, -31.75) * mm});
            skLineSegment(sketch, "E216.right", {"start": v(-17.46, 0) * mm, "end": v(-17.46, -31.75) * mm});
            skLineSegment(sketch, "E217.top", {"start": v(-18.96, -34.75) * mm, "end": v(-17.46, -34.75) * mm});
            skLineSegment(sketch, "E217.left", {"start": v(-18.96, -63.5) * mm, "end": v(-18.96, -34.75) * mm});
            skLineSegment(sketch, "E217.right", {"start": v(-17.46, -63.5) * mm, "end": v(-17.46, -34.75) * mm});
            skLineSegment(sketch, "E218", {"start": v(-17.46, -63.5) * mm, "end": v(-17.46, -65) * mm});
            skLineSegment(sketch, "E219.trimOffspring", {"start": v(-18.96, -65) * mm, "end": v(-23.46, -65) * mm});
            skLineSegment(sketch, "E220.trimOffspring", {"start": v(-17.46, 0) * mm, "end": v(-14.46, 0) * mm});
            skLineSegment(sketch, "E221.bottom", {"start": v(-17.46, -65) * mm, "end": v(-15.96, -65) * mm});
            skLineSegment(sketch, "E221.left", {"start": v(-17.46, -65) * mm, "end": v(-17.46, -63.5) * mm});
            skLineSegment(sketch, "E222.bottom", {"start": v(-17.46, 0) * mm, "end": v(-15.96, 0) * mm});
            skLineSegment(sketch, "E222.left", {"start": v(-17.46, 0) * mm, "end": v(-17.46, -1.5) * mm});
            skLineSegment(sketch, "E223.bottom", {"start": v(-15.96, 0) * mm, "end": v(-14.46, 0) * mm});
            skLineSegment(sketch, "E224.bottom", {"start": v(-15.96, -65) * mm, "end": v(-14.46, -65) * mm});
            skLineSegment(sketch, "E225.trimOffspring", {"start": v(-15.96, -65) * mm, "end": v(-17.46, -65) * mm});
            skLineSegment(sketch, "E226.bottom", {"start": v(-15.96, -63.5) * mm, "end": v(-14.46, -63.5) * mm});
            skLineSegment(sketch, "E226.left", {"start": v(-15.96, -63.5) * mm, "end": v(-15.96, -34.75) * mm});
            skLineSegment(sketch, "E226.right", {"start": v(-14.46, -63.5) * mm, "end": v(-14.46, -34.75) * mm});
            skLineSegment(sketch, "E227.left", {"start": v(-15.96, -34.75) * mm, "end": v(-15.96, -3) * mm});
            skLineSegment(sketch, "E227.right", {"start": v(-14.46, -34.75) * mm, "end": v(-14.46, -3) * mm});
            skLineSegment(sketch, "E228.bottom", {"start": v(-15.96, -1.5) * mm, "end": v(-14.46, -1.5) * mm});
            skLineSegment(sketch, "E228.left", {"start": v(-15.96, -1.5) * mm, "end": v(-15.96, -3) * mm});
            skLineSegment(sketch, "E228.right", {"start": v(-14.46, -1.5) * mm, "end": v(-14.46, -3) * mm});
            skLineSegment(sketch, "E229.top", {"start": v(-14.46, -65) * mm, "end": v(-12.96, -65) * mm});
            skLineSegment(sketch, "E229.right", {"start": v(-12.96, -63.5) * mm, "end": v(-12.96, -65) * mm});
            skLineSegment(sketch, "E230.top", {"start": v(-14.46, 0) * mm, "end": v(-12.96, 0) * mm});
            skLineSegment(sketch, "E230.right", {"start": v(-12.96, -1.5) * mm, "end": v(-12.96, 0) * mm});
            skLineSegment(sketch, "E231.left", {"start": v(-12.96, 0) * mm, "end": v(-12.96, -31.75) * mm});
            skLineSegment(sketch, "E231.right", {"start": v(-11.46, 0) * mm, "end": v(-11.46, -31.75) * mm});
            skLineSegment(sketch, "E232.trimOffspring", {"start": v(-11.46, 0) * mm, "end": v(-6.96, 0) * mm});
            skLineSegment(sketch, "E233.trimOffspring", {"start": v(-12.96, -65) * mm, "end": v(-14.46, -65) * mm});
            skLineSegment(sketch, "E234.trimOffspring", {"start": v(-12.96, -34.75) * mm, "end": v(-12.96, -65) * mm});
            skLineSegment(sketch, "E235.trimOffspring", {"start": v(-11.46, -34.75) * mm, "end": v(-11.46, -65) * mm});
            skLineSegment(sketch, "E236.bottom", {"start": v(-11.46, -65) * mm, "end": v(-9.96, -65) * mm});
            skLineSegment(sketch, "E236.left", {"start": v(-11.46, -65) * mm, "end": v(-11.46, -63.5) * mm});
            skLineSegment(sketch, "E237.bottom", {"start": v(-11.46, 0) * mm, "end": v(-9.96, 0) * mm});
            skLineSegment(sketch, "E237.left", {"start": v(-11.46, 0) * mm, "end": v(-11.46, -1.5) * mm});
            skLineSegment(sketch, "E238.bottom", {"start": v(-9.96, -1.5) * mm, "end": v(-8.46, -1.5) * mm});
            skLineSegment(sketch, "E238.top", {"start": v(-9.96, -63.5) * mm, "end": v(-8.46, -63.5) * mm});
            skLineSegment(sketch, "E238.left", {"start": v(-9.96, -1.5) * mm, "end": v(-9.96, -63.5) * mm});
            skLineSegment(sketch, "E238.right", {"start": v(-8.46, -1.5) * mm, "end": v(-8.46, -63.5) * mm});
            skLineSegment(sketch, "E239.trimOffspring", {"start": v(-11.46, -31.75) * mm, "end": v(-12.96, -31.75) * mm});
            skLineSegment(sketch, "E240.trimOffspring", {"start": v(-11.46, -34.75) * mm, "end": v(-12.96, -34.75) * mm});
            skPoint(sketch, "E241.top.end.orphan", {"position": v(-9.96, -63.5) * mm});
            skLineSegment(sketch, "E242.top", {"start": v(-8.46, -65) * mm, "end": v(-6.96, -65) * mm});
            skLineSegment(sketch, "E243.left", {"start": v(-6.96, -65) * mm, "end": v(-6.96, -34.75) * mm});
            skLineSegment(sketch, "E243.right", {"start": v(-5.46, -65) * mm, "end": v(-5.46, -34.75) * mm});
            skLineSegment(sketch, "E244.top", {"start": v(-8.46, 0) * mm, "end": v(-6.96, 0) * mm});
            skLineSegment(sketch, "E244.right", {"start": v(-6.96, -1.5) * mm, "end": v(-6.96, 0) * mm});
            skLineSegment(sketch, "E245.top", {"start": v(-6.96, -31.75) * mm, "end": v(-5.46, -31.75) * mm});
            skLineSegment(sketch, "E245.left", {"start": v(-6.96, -1.5) * mm, "end": v(-6.96, -31.75) * mm});
            skLineSegment(sketch, "E245.right", {"start": v(-5.46, -1.5) * mm, "end": v(-5.46, -31.75) * mm});
            skLineSegment(sketch, "E246", {"start": v(-5.46, -1.5) * mm, "end": v(-5.46, 0) * mm});
            skLineSegment(sketch, "E247.trimOffspring", {"start": v(-5.46, 0) * mm, "end": v(-0.96, 0) * mm});
            skLineSegment(sketch, "E248.bottom", {"start": v(-5.46, -65) * mm, "end": v(-3.96, -65) * mm});
            skLineSegment(sketch, "E248.left", {"start": v(-5.46, -65) * mm, "end": v(-5.46, -63.5) * mm});
            skLineSegment(sketch, "E249.bottom", {"start": v(-5.46, 0) * mm, "end": v(-3.96, 0) * mm});
            skLineSegment(sketch, "E249.left", {"start": v(-5.46, 0) * mm, "end": v(-5.46, -1.5) * mm});
            skLineSegment(sketch, "E250.bottom", {"start": v(-3.96, -1.5) * mm, "end": v(-2.46, -1.5) * mm});
            skLineSegment(sketch, "E250.top", {"start": v(-3.96, -63.5) * mm, "end": v(-2.46, -63.5) * mm});
            skLineSegment(sketch, "E250.left", {"start": v(-3.96, -1.5) * mm, "end": v(-3.96, -63.5) * mm});
            skLineSegment(sketch, "E250.right", {"start": v(-2.46, -1.5) * mm, "end": v(-2.46, -63.5) * mm});
            skLineSegment(sketch, "E251.trimOffspring", {"start": v(-5.46, -31.75) * mm, "end": v(-6.96, -31.75) * mm});
            skLineSegment(sketch, "E252.top", {"start": v(-2.46, -65) * mm, "end": v(-0.96, -65) * mm});
            skLineSegment(sketch, "E253.top", {"start": v(-2.46, 0) * mm, "end": v(-0.96, 0) * mm});
            skLineSegment(sketch, "E254.top", {"start": v(-0.96, -31.75) * mm, "end": v(0.54, -31.75) * mm});
            skLineSegment(sketch, "E254.left", {"start": v(-0.96, -1.5) * mm, "end": v(-0.96, -31.75) * mm});
            skLineSegment(sketch, "E254.right", {"start": v(0.54, -1.5) * mm, "end": v(0.54, -31.75) * mm});
            skLineSegment(sketch, "E255", {"start": v(-0.96, -1.5) * mm, "end": v(-0.96, 0) * mm});
            skLineSegment(sketch, "E256", {"start": v(0.54, -1.5) * mm, "end": v(0.54, 0) * mm});
            skLineSegment(sketch, "E257.trimOffspring", {"start": v(0.54, 0) * mm, "end": v(3.54, 0) * mm});
            skPoint(sketch, "E252.right.start.orphan", {"position": v(-0.96, -63.5) * mm});
            skLineSegment(sketch, "E258.left", {"start": v(-0.96, -65) * mm, "end": v(-0.96, -34.75) * mm});
            skLineSegment(sketch, "E258.right", {"start": v(0.54, -65) * mm, "end": v(0.54, -34.75) * mm});
            skLineSegment(sketch, "E259.trimOffspring", {"start": v(-0.96, -65) * mm, "end": v(-5.46, -65) * mm});
            skLineSegment(sketch, "E260.bottom", {"start": v(0.54, -65) * mm, "end": v(2.04, -65) * mm});
            skLineSegment(sketch, "E260.left", {"start": v(0.54, -65) * mm, "end": v(0.54, -63.5) * mm});
            skLineSegment(sketch, "E261.bottom", {"start": v(0.54, 0) * mm, "end": v(2.04, 0) * mm});
            skLineSegment(sketch, "E261.left", {"start": v(0.54, 0) * mm, "end": v(0.54, -1.5) * mm});
            skLineSegment(sketch, "E262.bottom", {"start": v(2.04, -1.5) * mm, "end": v(3.54, -1.5) * mm});
            skLineSegment(sketch, "E262.top", {"start": v(2.04, -63.5) * mm, "end": v(3.54, -63.5) * mm});
            skLineSegment(sketch, "E262.left", {"start": v(2.04, -1.5) * mm, "end": v(2.04, -63.5) * mm});
            skLineSegment(sketch, "E262.right", {"start": v(3.54, -1.5) * mm, "end": v(3.54, -63.5) * mm});
            skLineSegment(sketch, "E263.trimOffspring", {"start": v(0.54, -31.75) * mm, "end": v(-0.96, -31.75) * mm});
            skLineSegment(sketch, "E264.top", {"start": v(3.54, -65) * mm, "end": v(5.04, -65) * mm});
            skLineSegment(sketch, "E264.right", {"start": v(5.04, -63.5) * mm, "end": v(5.04, -65) * mm});
            skLineSegment(sketch, "E265.left", {"start": v(5.04, -63.5) * mm, "end": v(5.04, -34.75) * mm});
            skLineSegment(sketch, "E265.right", {"start": v(6.54, -65) * mm, "end": v(6.54, -34.75) * mm});
            skLineSegment(sketch, "E266.trimOffspring", {"start": v(5.04, -65) * mm, "end": v(0.54, -65) * mm});
            skLineSegment(sketch, "E267.top", {"start": v(3.54, 0) * mm, "end": v(5.04, 0) * mm});
            skLineSegment(sketch, "E267.right", {"start": v(5.04, -1.5) * mm, "end": v(5.04, 0) * mm});
            skLineSegment(sketch, "E268.top", {"start": v(5.04, -31.75) * mm, "end": v(6.54, -31.75) * mm});
            skLineSegment(sketch, "E268.left", {"start": v(5.04, -1.5) * mm, "end": v(5.04, -31.75) * mm});
            skLineSegment(sketch, "E268.right", {"start": v(6.54, -1.5) * mm, "end": v(6.54, -31.75) * mm});
            skLineSegment(sketch, "E269", {"start": v(6.54, -1.5) * mm, "end": v(6.54, 0) * mm});
            skLineSegment(sketch, "E270.trimOffspring", {"start": v(6.54, 0) * mm, "end": v(11.04, 0) * mm});
            skLineSegment(sketch, "E271.bottom", {"start": v(6.54, -65) * mm, "end": v(8.04, -65) * mm});
            skLineSegment(sketch, "E271.left", {"start": v(6.54, -65) * mm, "end": v(6.54, -63.5) * mm});
            skLineSegment(sketch, "E272.bottom", {"start": v(6.54, 0) * mm, "end": v(8.04, 0) * mm});
            skLineSegment(sketch, "E272.left", {"start": v(6.54, 0) * mm, "end": v(6.54, -1.5) * mm});
            skLineSegment(sketch, "E273.bottom", {"start": v(8.04, -1.5) * mm, "end": v(9.54, -1.5) * mm});
            skLineSegment(sketch, "E273.top", {"start": v(8.04, -63.5) * mm, "end": v(9.54, -63.5) * mm});
            skLineSegment(sketch, "E273.left", {"start": v(8.04, -1.5) * mm, "end": v(8.04, -31.75) * mm});
            skLineSegment(sketch, "E273.right", {"start": v(9.54, -1.5) * mm, "end": v(9.54, -31.75) * mm});
            skLineSegment(sketch, "E274.trimOffspring", {"start": v(6.54, -31.75) * mm, "end": v(5.04, -31.75) * mm});
            skLineSegment(sketch, "E275.top", {"start": v(9.54, -65) * mm, "end": v(11.04, -65) * mm});
            skLineSegment(sketch, "E275.right", {"start": v(11.04, -63.5) * mm, "end": v(11.04, -65) * mm});
            skLineSegment(sketch, "E276.left", {"start": v(11.04, -65) * mm, "end": v(11.04, -34.75) * mm});
            skLineSegment(sketch, "E276.right", {"start": v(12.54, -65) * mm, "end": v(12.54, -34.75) * mm});
            skLineSegment(sketch, "E277.trimOffspring", {"start": v(11.04, -65) * mm, "end": v(6.54, -65) * mm});
            skLineSegment(sketch, "E278.top", {"start": v(9.54, 0) * mm, "end": v(11.04, 0) * mm});
            skLineSegment(sketch, "E278.right", {"start": v(11.04, -1.5) * mm, "end": v(11.04, 0) * mm});
            skLineSegment(sketch, "E279.top", {"start": v(11.04, -31.75) * mm, "end": v(12.54, -31.75) * mm});
            skLineSegment(sketch, "E279.left", {"start": v(11.04, 0) * mm, "end": v(11.04, -31.75) * mm});
            skLineSegment(sketch, "E279.right", {"start": v(12.54, 0) * mm, "end": v(12.54, -31.75) * mm});
            skLineSegment(sketch, "E280.trimOffspring", {"start": v(12.54, 0) * mm, "end": v(17.04, 0) * mm});
            skLineSegment(sketch, "E281.bottom", {"start": v(12.54, -65) * mm, "end": v(14.04, -65) * mm});
            skLineSegment(sketch, "E281.left", {"start": v(12.54, -65) * mm, "end": v(12.54, -63.5) * mm});
            skLineSegment(sketch, "E282.bottom", {"start": v(12.54, 0) * mm, "end": v(14.04, 0) * mm});
            skLineSegment(sketch, "E282.left", {"start": v(12.54, 0) * mm, "end": v(12.54, -1.5) * mm});
            skLineSegment(sketch, "E283.bottom", {"start": v(14.04, -1.5) * mm, "end": v(15.54, -1.5) * mm});
            skLineSegment(sketch, "E283.top", {"start": v(14.04, -63.5) * mm, "end": v(15.54, -63.5) * mm});
            skLineSegment(sketch, "E283.right", {"start": v(15.54, -1.5) * mm, "end": v(15.54, -31.75) * mm});
            skPoint(sketch, "E281.right.end.orphan", {"position": v(14.04, -63.5) * mm});
            skLineSegment(sketch, "E284.trimOffspring", {"start": v(12.54, -31.75) * mm, "end": v(11.04, -31.75) * mm});
            skLineSegment(sketch, "E285.top", {"start": v(15.54, -65) * mm, "end": v(17.04, -65) * mm});
            skLineSegment(sketch, "E286.top", {"start": v(15.54, 0) * mm, "end": v(17.04, 0) * mm});
            skLineSegment(sketch, "E286.right", {"start": v(17.04, -1.5) * mm, "end": v(17.04, 0) * mm});
            skLineSegment(sketch, "E287.top", {"start": v(17.04, -31.75) * mm, "end": v(18.54, -31.75) * mm});
            skLineSegment(sketch, "E287.left", {"start": v(17.04, -1.5) * mm, "end": v(17.04, -31.75) * mm});
            skLineSegment(sketch, "E287.right", {"start": v(18.54, -1.5) * mm, "end": v(18.54, -31.75) * mm});
            skLineSegment(sketch, "E288", {"start": v(18.54, -1.5) * mm, "end": v(18.54, 0) * mm});
            skLineSegment(sketch, "E289.trimOffspring", {"start": v(18.54, 0) * mm, "end": v(21.54, 0) * mm});
            skLineSegment(sketch, "E290.right", {"start": v(17.04, -65) * mm, "end": v(17.04, -63.5) * mm});
            skLineSegment(sketch, "E291.top", {"start": v(17.04, -34.75) * mm, "end": v(18.54, -34.75) * mm});
            skLineSegment(sketch, "E291.left", {"start": v(17.04, -65) * mm, "end": v(17.04, -34.75) * mm});
            skLineSegment(sketch, "E291.right", {"start": v(18.54, -65) * mm, "end": v(18.54, -34.75) * mm});
            skLineSegment(sketch, "E292.trimOffspring", {"start": v(15.54, -65) * mm, "end": v(12.54, -65) * mm});
            skLineSegment(sketch, "E293.bottom", {"start": v(18.54, -65) * mm, "end": v(20.04, -65) * mm});
            skLineSegment(sketch, "E293.left", {"start": v(18.54, -65) * mm, "end": v(18.54, -63.5) * mm});
            skLineSegment(sketch, "E294.bottom", {"start": v(18.54, 0) * mm, "end": v(20.04, 0) * mm});
            skLineSegment(sketch, "E294.left", {"start": v(18.54, 0) * mm, "end": v(18.54, -1.5) * mm});
            skLineSegment(sketch, "E295.bottom", {"start": v(20.04, -1.5) * mm, "end": v(21.54, -1.5) * mm});
            skLineSegment(sketch, "E295.top", {"start": v(20.04, -63.5) * mm, "end": v(21.54, -63.5) * mm});
            skLineSegment(sketch, "E295.left", {"start": v(20.04, -1.5) * mm, "end": v(20.04, -34.75) * mm});
            skLineSegment(sketch, "E295.right", {"start": v(21.54, -1.5) * mm, "end": v(21.54, -34.75) * mm});
            skPoint(sketch, "E293.top.end.orphan", {"position": v(20.04, -63.5) * mm});
            skLineSegment(sketch, "E296.trimOffspring", {"start": v(18.54, -31.75) * mm, "end": v(17.04, -31.75) * mm});
            skLineSegment(sketch, "E297.trimOffspring", {"start": v(-5.46, -34.75) * mm, "end": v(-6.96, -34.75) * mm});
            skLineSegment(sketch, "E298.trimOffspring", {"start": v(0.54, -34.75) * mm, "end": v(-0.96, -34.75) * mm});
            skLineSegment(sketch, "E299.trimOffspring", {"start": v(6.54, -34.75) * mm, "end": v(5.04, -34.75) * mm});
            skLineSegment(sketch, "E300.trimOffspring", {"start": v(12.54, -34.75) * mm, "end": v(11.04, -34.75) * mm});
            skLineSegment(sketch, "E301.trimOffspring", {"start": v(18.54, -34.75) * mm, "end": v(17.04, -34.75) * mm});
            skLineSegment(sketch, "E302.trimOffspring", {"start": v(17.04, -65) * mm, "end": v(12.54, -65) * mm});
            skLineSegment(sketch, "E303.trimOffspring", {"start": v(11.04, -65) * mm, "end": v(8.04, -65) * mm});
            skLineSegment(sketch, "E304.trimOffspring", {"start": v(5.04, -65) * mm, "end": v(2.04, -65) * mm});
            skLineSegment(sketch, "E305.top", {"start": v(21.54, -65) * mm, "end": v(23.04, -65) * mm});
            skLineSegment(sketch, "E305.right", {"start": v(23.04, -63.5) * mm, "end": v(23.04, -65) * mm});
            skLineSegment(sketch, "E306.top", {"start": v(21.54, 0) * mm, "end": v(23.04, 0) * mm});
            skLineSegment(sketch, "E306.right", {"start": v(23.04, -1.5) * mm, "end": v(23.04, 0) * mm});
            skLineSegment(sketch, "E307.top", {"start": v(23.04, -34.75) * mm, "end": v(24.54, -34.75) * mm});
            skLineSegment(sketch, "E307.left", {"start": v(23.04, -63.5) * mm, "end": v(23.04, -34.75) * mm});
            skLineSegment(sketch, "E307.right", {"start": v(24.54, -63.5) * mm, "end": v(24.54, -34.75) * mm});
            skLineSegment(sketch, "E308.top", {"start": v(23.04, -31.75) * mm, "end": v(24.54, -31.75) * mm});
            skLineSegment(sketch, "E308.left", {"start": v(23.04, -1.5) * mm, "end": v(23.04, -31.75) * mm});
            skLineSegment(sketch, "E308.right", {"start": v(24.54, -1.5) * mm, "end": v(24.54, -31.75) * mm});
            skLineSegment(sketch, "E309", {"start": v(24.54, -63.5) * mm, "end": v(24.54, -65) * mm});
            skLineSegment(sketch, "E310", {"start": v(24.54, -65) * mm, "end": v(24.54, -34.75) * mm});
            skLineSegment(sketch, "E311", {"start": v(24.54, -1.5) * mm, "end": v(24.54, 0) * mm});
            skLineSegment(sketch, "E312.trimOffspring", {"start": v(24.54, 0) * mm, "end": v(27.54, 0) * mm});
            skLineSegment(sketch, "E313.trimOffspring", {"start": v(23.04, -65) * mm, "end": v(18.54, -65) * mm});
            skLineSegment(sketch, "E314.trimOffspring", {"start": v(23.04, -65) * mm, "end": v(20.04, -65) * mm});
            skLineSegment(sketch, "E315.trimOffspring", {"start": v(24.54, -31.75) * mm, "end": v(24.54, -1.5) * mm});
            skLineSegment(sketch, "E316.bottom", {"start": v(24.54, -65) * mm, "end": v(26.04, -65) * mm});
            skLineSegment(sketch, "E316.left", {"start": v(24.54, -65) * mm, "end": v(24.54, -63.5) * mm});
            skLineSegment(sketch, "E317.bottom", {"start": v(24.54, 0) * mm, "end": v(26.04, 0) * mm});
            skLineSegment(sketch, "E317.left", {"start": v(24.54, 0) * mm, "end": v(24.54, -1.5) * mm});
            skLineSegment(sketch, "E318.bottom", {"start": v(26.04, -1.5) * mm, "end": v(27.54, -1.5) * mm});
            skLineSegment(sketch, "E318.top", {"start": v(26.04, -63.5) * mm, "end": v(27.54, -63.5) * mm});
            skLineSegment(sketch, "E318.right", {"start": v(27.54, -1.5) * mm, "end": v(27.54, -31.75) * mm});
            skLineSegment(sketch, "E319.trimOffspring", {"start": v(24.54, -34.75) * mm, "end": v(23.04, -34.75) * mm});
            skLineSegment(sketch, "E320.trimOffspring", {"start": v(24.54, -31.75) * mm, "end": v(23.04, -31.75) * mm});
            skLineSegment(sketch, "E321.top", {"start": v(27.54, -65) * mm, "end": v(29.04, -65) * mm});
            skLineSegment(sketch, "E322.top", {"start": v(27.54, 0) * mm, "end": v(29.04, 0) * mm});
            skLineSegment(sketch, "E322.right", {"start": v(29.04, -1.5) * mm, "end": v(29.04, 0) * mm});
            skLineSegment(sketch, "E323.top", {"start": v(29.04, -31.75) * mm, "end": v(30.54, -31.75) * mm});
            skLineSegment(sketch, "E323.left", {"start": v(29.04, -1.5) * mm, "end": v(29.04, -31.75) * mm});
            skLineSegment(sketch, "E323.right", {"start": v(30.54, 0) * mm, "end": v(30.54, -31.75) * mm});
            skLineSegment(sketch, "E324.top", {"start": v(29.04, -34.75) * mm, "end": v(30.54, -34.75) * mm});
            skLineSegment(sketch, "E324.left", {"start": v(29.04, -65) * mm, "end": v(29.04, -34.75) * mm});
            skLineSegment(sketch, "E324.right", {"start": v(30.54, -65) * mm, "end": v(30.54, -34.75) * mm});
            skLineSegment(sketch, "E325.trimOffspring", {"start": v(29.04, -65) * mm, "end": v(24.54, -65) * mm});
            skLineSegment(sketch, "E326.trimOffspring", {"start": v(30.54, 0) * mm, "end": v(35.04, 0) * mm});
            skLineSegment(sketch, "E327.bottom", {"start": v(30.54, -65) * mm, "end": v(32.04, -65) * mm});
            skLineSegment(sketch, "E327.left", {"start": v(30.54, -65) * mm, "end": v(30.54, -63.5) * mm});
            skLineSegment(sketch, "E328.bottom", {"start": v(30.54, 0) * mm, "end": v(32.04, 0) * mm});
            skLineSegment(sketch, "E328.left", {"start": v(30.54, 0) * mm, "end": v(30.54, -1.5) * mm});
            skLineSegment(sketch, "E329.bottom", {"start": v(32.04, -1.5) * mm, "end": v(33.54, -1.5) * mm});
            skLineSegment(sketch, "E329.top", {"start": v(32.04, -63.5) * mm, "end": v(33.54, -63.5) * mm});
            skLineSegment(sketch, "E329.right", {"start": v(33.54, -1.5) * mm, "end": v(33.54, -31.75) * mm});
            skPoint(sketch, "E327.right.end.orphan", {"position": v(32.04, -63.5) * mm});
            skLineSegment(sketch, "E330.top", {"start": v(33.54, -65) * mm, "end": v(35.04, -65) * mm});
            skLineSegment(sketch, "E330.right", {"start": v(35.04, -63.5) * mm, "end": v(35.04, -65) * mm});
            skLineSegment(sketch, "E331.top", {"start": v(33.54, 0) * mm, "end": v(35.04, 0) * mm});
            skLineSegment(sketch, "E331.right", {"start": v(35.04, -1.5) * mm, "end": v(35.04, 0) * mm});
            skLineSegment(sketch, "E332.top", {"start": v(35.04, -31.75) * mm, "end": v(36.54, -31.75) * mm});
            skLineSegment(sketch, "E332.left", {"start": v(35.04, 0) * mm, "end": v(35.04, -31.75) * mm});
            skLineSegment(sketch, "E332.right", {"start": v(36.54, 0) * mm, "end": v(36.54, -31.75) * mm});
            skLineSegment(sketch, "E333.top", {"start": v(35.04, -34.75) * mm, "end": v(36.54, -34.75) * mm});
            skLineSegment(sketch, "E333.left", {"start": v(35.04, -63.5) * mm, "end": v(35.04, -34.75) * mm});
            skLineSegment(sketch, "E333.right", {"start": v(36.54, -63.5) * mm, "end": v(36.54, -34.75) * mm});
            skLineSegment(sketch, "E334", {"start": v(36.54, -63.5) * mm, "end": v(36.54, -65) * mm});
            skLineSegment(sketch, "E335.trimOffspring", {"start": v(35.04, -65) * mm, "end": v(32.04, -65) * mm});
            skLineSegment(sketch, "E336.trimOffspring", {"start": v(36.54, 0) * mm, "end": v(39.54, 0) * mm});
            skLineSegment(sketch, "E337.bottom", {"start": v(36.54, -65) * mm, "end": v(38.04, -65) * mm});
            skLineSegment(sketch, "E337.left", {"start": v(36.54, -65) * mm, "end": v(36.54, -63.5) * mm});
            skLineSegment(sketch, "E338.bottom", {"start": v(36.54, 0) * mm, "end": v(38.04, 0) * mm});
            skLineSegment(sketch, "E338.left", {"start": v(36.54, 0) * mm, "end": v(36.54, -1.5) * mm});
            skLineSegment(sketch, "E339.bottom", {"start": v(38.04, 0) * mm, "end": v(39.54, 0) * mm});
            skLineSegment(sketch, "E340.bottom", {"start": v(38.04, -65) * mm, "end": v(39.54, -65) * mm});
            skLineSegment(sketch, "E341.trimOffspring", {"start": v(38.04, -65) * mm, "end": v(36.54, -65) * mm});
            skLineSegment(sketch, "E342.left", {"start": v(38.04, -63.5) * mm, "end": v(38.04, -34.75) * mm});
            skLineSegment(sketch, "E342.right", {"start": v(39.54, -63.5) * mm, "end": v(39.54, -34.75) * mm});
            skLineSegment(sketch, "E343.bottom", {"start": v(38.04, -1.5) * mm, "end": v(39.54, -1.5) * mm});
            skLineSegment(sketch, "E343.left", {"start": v(38.04, -1.5) * mm, "end": v(38.04, -3) * mm});
            skLineSegment(sketch, "E343.right", {"start": v(39.54, -1.5) * mm, "end": v(39.54, -3) * mm});
            skLineSegment(sketch, "E344.top", {"start": v(39.54, -65) * mm, "end": v(41.04, -65) * mm});
            skLineSegment(sketch, "E344.right", {"start": v(41.04, -63.5) * mm, "end": v(41.04, -65) * mm});
            skLineSegment(sketch, "E345.top", {"start": v(39.54, 0) * mm, "end": v(41.04, 0) * mm});
            skLineSegment(sketch, "E345.right", {"start": v(41.04, -1.5) * mm, "end": v(41.04, 0) * mm});
            skLineSegment(sketch, "E346.left", {"start": v(41.04, 0) * mm, "end": v(41.04, -31.75) * mm});
            skLineSegment(sketch, "E346.right", {"start": v(42.54, 0) * mm, "end": v(42.54, -31.75) * mm});
            skLineSegment(sketch, "E347.trimOffspring", {"start": v(41.04, -65) * mm, "end": v(39.54, -65) * mm});
            skLineSegment(sketch, "E348.trimOffspring", {"start": v(41.04, -34.75) * mm, "end": v(41.04, -65) * mm});
            skLineSegment(sketch, "E349.trimOffspring", {"start": v(42.54, -34.75) * mm, "end": v(42.54, -65) * mm});
            skLineSegment(sketch, "E350.bottom", {"start": v(42.54, -65) * mm, "end": v(44.04, -65) * mm});
            skLineSegment(sketch, "E350.left", {"start": v(42.54, -65) * mm, "end": v(42.54, -63.5) * mm});
            skLineSegment(sketch, "E351.bottom", {"start": v(42.54, 0) * mm, "end": v(44.04, 0) * mm});
            skLineSegment(sketch, "E351.left", {"start": v(42.54, 0) * mm, "end": v(42.54, -1.5) * mm});
            skLineSegment(sketch, "E352.bottom", {"start": v(44.04, -1.5) * mm, "end": v(45.54, -1.5) * mm});
            skLineSegment(sketch, "E352.top", {"start": v(44.04, -63.5) * mm, "end": v(45.54, -63.5) * mm});
            skLineSegment(sketch, "E352.left", {"start": v(44.04, -1.5) * mm, "end": v(44.04, -31.75) * mm});
            skLineSegment(sketch, "E352.right", {"start": v(45.54, -1.5) * mm, "end": v(45.54, -31.75) * mm});
            skLineSegment(sketch, "E353.trimOffspring", {"start": v(42.54, -31.75) * mm, "end": v(41.04, -31.75) * mm});
            skLineSegment(sketch, "E354.trimOffspring", {"start": v(42.54, -34.75) * mm, "end": v(41.04, -34.75) * mm});
            skLineSegment(sketch, "E355.trimOffspring", {"start": v(-6.96, -65) * mm, "end": v(-11.46, -65) * mm});
            skLineSegment(sketch, "E356.trimOffspring", {"start": v(-0.96, -65) * mm, "end": v(-3.96, -65) * mm});
            skLineSegment(sketch, "E357.trimOffspring", {"start": v(0.54, 0) * mm, "end": v(5.04, 0) * mm});
            skLineSegment(sketch, "E358.trimOffspring", {"start": v(18.54, -65) * mm, "end": v(23.04, -65) * mm});
            skLineSegment(sketch, "E359.trimOffspring", {"start": v(24.54, -65) * mm, "end": v(27.54, -65) * mm});
            skLineSegment(sketch, "E360.trimOffspring", {"start": v(30.54, -65) * mm, "end": v(33.54, -65) * mm});
            skLineSegment(sketch, "E361.trimOffspring", {"start": v(36.54, -65) * mm, "end": v(41.04, -65) * mm});
            skLineSegment(sketch, "E362.trimOffspring", {"start": v(42.54, -65) * mm, "end": v(45.54, -65) * mm});
            skLineSegment(sketch, "E363.trimOffspring", {"start": v(42.54, 0) * mm, "end": v(45.54, 0) * mm});
            skLineSegment(sketch, "E364.trimOffspring", {"start": v(36.54, 0) * mm, "end": v(41.04, 0) * mm});
            skLineSegment(sketch, "E365.trimOffspring", {"start": v(24.54, 0) * mm, "end": v(29.04, 0) * mm});
            skLineSegment(sketch, "E366.trimOffspring", {"start": v(12.54, 0) * mm, "end": v(13.44, 0) * mm});
            skPoint(sketch, "E367.top.end.orphan", {"position": v(5.04, -63.5) * mm});
            skLineSegment(sketch, "E368.left", {"start": v(11.04, -1.5) * mm, "end": v(11.04, -31.75) * mm});
            skLineSegment(sketch, "E369.left", {"start": v(14.04, -1.5) * mm, "end": v(14.04, -31.75) * mm});
            skLineSegment(sketch, "E370.left", {"start": v(14.04, -63.5) * mm, "end": v(14.04, -34.75) * mm});
            skLineSegment(sketch, "E370.right", {"start": v(15.54, -63.5) * mm, "end": v(15.54, -34.75) * mm});
            skLineSegment(sketch, "E371.left", {"start": v(20.04, -63.5) * mm, "end": v(20.04, -34.75) * mm});
            skLineSegment(sketch, "E371.right", {"start": v(21.54, -63.5) * mm, "end": v(21.54, -34.75) * mm});
            skLineSegment(sketch, "E372.trimOffspring", {"start": v(20.04, -65) * mm, "end": v(18.54, -65) * mm});
            skLineSegment(sketch, "E373.left", {"start": v(26.04, -63.5) * mm, "end": v(26.04, -34.75) * mm});
            skLineSegment(sketch, "E373.right", {"start": v(27.54, -63.5) * mm, "end": v(27.54, -34.75) * mm});
            skLineSegment(sketch, "E374.trimOffspring", {"start": v(26.04, -65) * mm, "end": v(24.54, -65) * mm});
            skLineSegment(sketch, "E375.left", {"start": v(26.04, -1.5) * mm, "end": v(26.04, -31.75) * mm});
            skPoint(sketch, "E376.right.end.orphan", {"position": v(29.04, -63.5) * mm});
            skLineSegment(sketch, "E377.left", {"start": v(32.04, -1.5) * mm, "end": v(32.04, -31.75) * mm});
            skLineSegment(sketch, "E378.trimOffspring", {"start": v(29.04, -65) * mm, "end": v(27.54, -65) * mm});
            skPoint(sketch, "E379.top.end.orphan", {"position": v(35.04, -63.5) * mm});
            skLineSegment(sketch, "E380.trimOffspring", {"start": v(14.04, -65) * mm, "end": v(12.54, -65) * mm});
            skLineSegment(sketch, "E381.left", {"start": v(38.04, -1.5) * mm, "end": v(38.04, -31.75) * mm});
            skLineSegment(sketch, "E381.right", {"start": v(39.54, -1.5) * mm, "end": v(39.54, -31.75) * mm});
            skLineSegment(sketch, "E382.trimOffspring", {"start": v(39.54, -31.75) * mm, "end": v(39.54, -1.5) * mm});
            skLineSegment(sketch, "E383.bottom", {"start": v(45.54, -65) * mm, "end": v(47.04, -65) * mm});
            skLineSegment(sketch, "E384.bottom", {"start": v(45.54, 0) * mm, "end": v(47.04, 0) * mm});
            skLineSegment(sketch, "E385.left", {"start": v(47.04, -1.5) * mm, "end": v(47.04, -31.75) * mm});
            skLineSegment(sketch, "E385.right", {"start": v(48.54, -1.5) * mm, "end": v(48.54, -31.75) * mm});
            skPoint(sketch, "E383.right.end.orphan", {"position": v(47.04, -63.5) * mm});
            skLineSegment(sketch, "E386.top", {"start": v(48.54, -65) * mm, "end": v(50.04, -65) * mm});
            skLineSegment(sketch, "E387.top", {"start": v(48.54, 0) * mm, "end": v(50.04, 0) * mm});
            skLineSegment(sketch, "E388.left", {"start": v(50.04, -1.5) * mm, "end": v(50.04, -31.75) * mm});
            skLineSegment(sketch, "E388.right", {"start": v(51.54, -1.5) * mm, "end": v(51.54, -31.75) * mm});
            skLineSegment(sketch, "E389.left", {"start": v(50.04, -63.5) * mm, "end": v(50.04, -34.75) * mm});
            skLineSegment(sketch, "E389.right", {"start": v(51.54, -63.5) * mm, "end": v(51.54, -34.75) * mm});
            skLineSegment(sketch, "E390.trimOffspring", {"start": v(50.04, -65) * mm, "end": v(48.54, -65) * mm});
            skLineSegment(sketch, "E391.trimOffspring", {"start": v(51.54, 0) * mm, "end": v(53.04, 0) * mm});
            skLineSegment(sketch, "E392.bottom", {"start": v(51.54, -65) * mm, "end": v(53.04, -65) * mm});
            skLineSegment(sketch, "E393.trimOffspring", {"start": v(53.04, -65) * mm, "end": v(51.54, -65) * mm});
            skLineSegment(sketch, "E394.left", {"start": v(53.04, -63.5) * mm, "end": v(53.04, -34.75) * mm});
            skLineSegment(sketch, "E394.right", {"start": v(54.54, -63.5) * mm, "end": v(54.54, -34.75) * mm});
            skLineSegment(sketch, "E395.left", {"start": v(53.04, -31.75) * mm, "end": v(53.04, -3) * mm});
            skLineSegment(sketch, "E395.right", {"start": v(54.54, -31.75) * mm, "end": v(54.54, -3) * mm});
            skLineSegment(sketch, "E396.left", {"start": v(53.04, -1.5) * mm, "end": v(53.04, -3) * mm});
            skLineSegment(sketch, "E396.right", {"start": v(54.54, -1.5) * mm, "end": v(54.54, -3) * mm});
            skLineSegment(sketch, "E397.top", {"start": v(54.54, -65) * mm, "end": v(56.04, -65) * mm});
            skLineSegment(sketch, "E398.top", {"start": v(54.54, 0) * mm, "end": v(56.04, 0) * mm});
            skLineSegment(sketch, "E399.left", {"start": v(56.04, -1.5) * mm, "end": v(56.04, -31.75) * mm});
            skLineSegment(sketch, "E399.right", {"start": v(57.54, -1.5) * mm, "end": v(57.54, -31.75) * mm});
            skLineSegment(sketch, "E400.trimOffspring", {"start": v(56.04, -65) * mm, "end": v(54.54, -65) * mm});
            skLineSegment(sketch, "E401.trimOffspring", {"start": v(56.04, -34.75) * mm, "end": v(56.04, -63.5) * mm});
            skLineSegment(sketch, "E402.trimOffspring", {"start": v(57.54, -34.75) * mm, "end": v(57.54, -63.5) * mm});
            skLineSegment(sketch, "E403.bottom", {"start": v(57.54, -65) * mm, "end": v(59.04, -65) * mm});
            skLineSegment(sketch, "E404.bottom", {"start": v(57.54, 0) * mm, "end": v(59.04, 0) * mm});
            skLineSegment(sketch, "E405.left", {"start": v(59.04, -1.5) * mm, "end": v(59.04, -31.75) * mm});
            skLineSegment(sketch, "E405.right", {"start": v(60.54, -1.5) * mm, "end": v(60.54, -31.75) * mm});
            skLineSegment(sketch, "E406.trimOffspring", {"start": v(11.04, -65) * mm, "end": v(9.54, -65) * mm});
            skLineSegment(sketch, "E407.trimOffspring", {"start": v(15.94, -65) * mm, "end": v(15.54, -65) * mm});
            skLineSegment(sketch, "E408.trimOffspring", {"start": v(17.04, -65) * mm, "end": v(15.54, -65) * mm});
            skLineSegment(sketch, "E409.trimOffspring", {"start": v(23.04, -65) * mm, "end": v(21.54, -65) * mm});
            skLineSegment(sketch, "E410.trimOffspring", {"start": v(35.04, -65) * mm, "end": v(33.54, -65) * mm});
            skLineSegment(sketch, "E411", {"start": v(38.04, -63.5) * mm, "end": v(39.54, -63.5) * mm});
            skLineSegment(sketch, "E412", {"start": v(47.04, -63.5) * mm, "end": v(47.04, -65) * mm});
            skLineSegment(sketch, "E413", {"start": v(48.54, -63.5) * mm, "end": v(48.54, -65) * mm});
            skLineSegment(sketch, "E414.trimOffspring", {"start": v(48.54, -65) * mm, "end": v(53.04, -65) * mm});
            skLineSegment(sketch, "E415.trimOffspring", {"start": v(47.04, -65) * mm, "end": v(45.54, -65) * mm});
            skLineSegment(sketch, "E416", {"start": v(50.04, -63.5) * mm, "end": v(51.54, -63.5) * mm});
            skLineSegment(sketch, "E417", {"start": v(53.04, -63.5) * mm, "end": v(53.04, -65) * mm});
            skLineSegment(sketch, "E418", {"start": v(54.54, -63.5) * mm, "end": v(54.54, -65) * mm});
            skLineSegment(sketch, "E419.trimOffspring", {"start": v(54.54, -65) * mm, "end": v(57.54, -65) * mm});
            skLineSegment(sketch, "E420", {"start": v(56.04, -63.5) * mm, "end": v(57.54, -63.5) * mm});
            skLineSegment(sketch, "E421.trimOffspring", {"start": v(5.04, -34.75) * mm, "end": v(5.04, -63.5) * mm});
            skLineSegment(sketch, "E422.trimOffspring", {"start": v(6.54, -34.75) * mm, "end": v(6.54, -63.5) * mm});
            skLineSegment(sketch, "E423.trimOffspring", {"start": v(8.04, -34.75) * mm, "end": v(8.04, -63.5) * mm});
            skLineSegment(sketch, "E424.trimOffspring", {"start": v(9.54, -34.75) * mm, "end": v(9.54, -63.5) * mm});
            skLineSegment(sketch, "E425.trimOffspring", {"start": v(11.04, -34.75) * mm, "end": v(11.04, -63.5) * mm});
            skLineSegment(sketch, "E426.trimOffspring", {"start": v(12.54, -34.75) * mm, "end": v(12.54, -63.5) * mm});
            skLineSegment(sketch, "E427.trimOffspring", {"start": v(14.04, -34.75) * mm, "end": v(14.04, -63.5) * mm});
            skLineSegment(sketch, "E428.trimOffspring", {"start": v(15.54, -34.75) * mm, "end": v(15.54, -63.5) * mm});
            skLineSegment(sketch, "E429.trimOffspring", {"start": v(17.04, -34.75) * mm, "end": v(17.04, -63.5) * mm});
            skLineSegment(sketch, "E430.trimOffspring", {"start": v(18.54, -34.75) * mm, "end": v(18.54, -63.5) * mm});
            skLineSegment(sketch, "E431.trimOffspring", {"start": v(20.04, -34.75) * mm, "end": v(20.04, -63.5) * mm});
            skLineSegment(sketch, "E432.trimOffspring", {"start": v(21.54, -34.75) * mm, "end": v(21.54, -63.5) * mm});
            skLineSegment(sketch, "E433.trimOffspring", {"start": v(23.04, -34.75) * mm, "end": v(23.04, -63.5) * mm});
            skLineSegment(sketch, "E434.trimOffspring", {"start": v(24.54, -34.75) * mm, "end": v(24.54, -63.5) * mm});
            skLineSegment(sketch, "E435.trimOffspring", {"start": v(26.04, -34.75) * mm, "end": v(26.04, -63.5) * mm});
            skLineSegment(sketch, "E436.trimOffspring", {"start": v(27.54, -34.75) * mm, "end": v(27.54, -63.5) * mm});
            skLineSegment(sketch, "E437.trimOffspring", {"start": v(29.04, -34.75) * mm, "end": v(29.04, -63.5) * mm});
            skLineSegment(sketch, "E438.trimOffspring", {"start": v(30.54, -34.75) * mm, "end": v(30.54, -63.5) * mm});
            skLineSegment(sketch, "E439.trimOffspring", {"start": v(32.04, -34.75) * mm, "end": v(32.04, -63.5) * mm});
            skLineSegment(sketch, "E440.trimOffspring", {"start": v(33.54, -34.75) * mm, "end": v(33.54, -63.5) * mm});
            skLineSegment(sketch, "E441.trimOffspring", {"start": v(35.04, -34.75) * mm, "end": v(35.04, -63.5) * mm});
            skLineSegment(sketch, "E442.trimOffspring", {"start": v(36.54, -34.75) * mm, "end": v(36.54, -63.5) * mm});
            skLineSegment(sketch, "E443.trimOffspring", {"start": v(41.04, -34.75) * mm, "end": v(41.04, -63.5) * mm});
            skLineSegment(sketch, "E444.trimOffspring", {"start": v(42.54, -34.75) * mm, "end": v(42.54, -63.5) * mm});
            skLineSegment(sketch, "E445.trimOffspring", {"start": v(44.04, -34.75) * mm, "end": v(44.04, -63.5) * mm});
            skLineSegment(sketch, "E446.trimOffspring", {"start": v(45.54, -34.75) * mm, "end": v(45.54, -63.5) * mm});
            skLineSegment(sketch, "E447", {"start": v(8.04, -31.75) * mm, "end": v(8.04, -34.75) * mm});
            skLineSegment(sketch, "E448", {"start": v(9.54, -31.75) * mm, "end": v(9.54, -34.75) * mm});
            skLineSegment(sketch, "E449", {"start": v(14.04, -31.75) * mm, "end": v(14.04, -34.75) * mm});
            skLineSegment(sketch, "E450", {"start": v(15.54, -31.75) * mm, "end": v(15.54, -34.75) * mm});
            skLineSegment(sketch, "E451", {"start": v(20.04, -34.75) * mm, "end": v(20.04, -34.75) * mm});
            skLineSegment(sketch, "E452", {"start": v(47.04, -1.5) * mm, "end": v(47.04, 0) * mm});
            skLineSegment(sketch, "E453", {"start": v(48.54, 0) * mm, "end": v(48.54, -1.5) * mm});
            skLineSegment(sketch, "E454.trimOffspring", {"start": v(48.54, 0) * mm, "end": v(53.04, 0) * mm});
            skLineSegment(sketch, "E455", {"start": v(51.54, -1.5) * mm, "end": v(50.04, -1.5) * mm});
            skLineSegment(sketch, "E456", {"start": v(53.04, -1.5) * mm, "end": v(53.04, 0) * mm});
            skLineSegment(sketch, "E457", {"start": v(54.54, 0) * mm, "end": v(54.54, -1.5) * mm});
            skLineSegment(sketch, "E458.trimOffspring", {"start": v(54.54, 0) * mm, "end": v(59.04, 0) * mm});
            skLineSegment(sketch, "E459", {"start": v(56.04, -1.5) * mm, "end": v(57.54, -1.5) * mm});
            skLineSegment(sketch, "E460", {"start": v(26.04, -31.75) * mm, "end": v(26.04, -34.75) * mm});
            skLineSegment(sketch, "E461", {"start": v(27.54, -31.75) * mm, "end": v(27.54, -34.75) * mm});
            skLineSegment(sketch, "E462", {"start": v(32.04, -31.75) * mm, "end": v(32.04, -34.75) * mm});
            skLineSegment(sketch, "E463", {"start": v(33.54, -31.75) * mm, "end": v(33.54, -34.75) * mm});
            skLineSegment(sketch, "E464", {"start": v(38.04, -31.75) * mm, "end": v(38.04, -34.75) * mm});
            skLineSegment(sketch, "E465", {"start": v(39.54, -31.75) * mm, "end": v(39.54, -34.75) * mm});
            skLineSegment(sketch, "E466", {"start": v(44.04, -31.75) * mm, "end": v(44.04, -34.75) * mm});
            skLineSegment(sketch, "E467", {"start": v(45.54, -31.75) * mm, "end": v(45.54, -34.75) * mm});
            skLineSegment(sketch, "E468", {"start": v(50.04, -31.75) * mm, "end": v(50.04, -34.75) * mm});
            skLineSegment(sketch, "E469", {"start": v(51.54, -34.75) * mm, "end": v(51.54, -31.75) * mm});
            skLineSegment(sketch, "E470", {"start": v(56.04, -31.75) * mm, "end": v(56.04, -34.75) * mm});
            skLineSegment(sketch, "E471", {"start": v(57.54, -31.75) * mm, "end": v(57.54, -34.75) * mm});
            skLineSegment(sketch, "E472", {"start": v(60.54, -34.75) * mm, "end": v(59.04, -34.75) * mm});
            skLineSegment(sketch, "E473", {"start": v(59.04, -31.75) * mm, "end": v(60.54, -31.75) * mm});
            skLineSegment(sketch, "E474", {"start": v(59.04, -1.5) * mm, "end": v(59.04, 0) * mm});
            skLineSegment(sketch, "E475", {"start": v(60.54, -1.5) * mm, "end": v(60.54, 0) * mm});
            skLineSegment(sketch, "E476.trimOffspring", {"start": v(60.54, 0) * mm, "end": v(62.34, 0) * mm});
            skLineSegment(sketch, "E477", {"start": v(53.04, -34.75) * mm, "end": v(54.54, -34.75) * mm});
            skLineSegment(sketch, "E478", {"start": v(53.04, -31.75) * mm, "end": v(54.54, -31.75) * mm});
            skLineSegment(sketch, "E479.trimOffspring", {"start": v(59.04, -34.75) * mm, "end": v(59.04, -63.5) * mm});
            skLineSegment(sketch, "E480.trimOffspring", {"start": v(60.54, -34.75) * mm, "end": v(60.54, -63.5) * mm});
            skLineSegment(sketch, "E481", {"start": v(47.04, -31.75) * mm, "end": v(48.54, -31.75) * mm});
            skLineSegment(sketch, "E482", {"start": v(47.04, -34.75) * mm, "end": v(48.54, -34.75) * mm});
            skLineSegment(sketch, "E483.trimOffspring", {"start": v(47.04, -34.75) * mm, "end": v(47.04, -63.5) * mm});
            skLineSegment(sketch, "E484.trimOffspring", {"start": v(48.54, -34.75) * mm, "end": v(48.54, -63.5) * mm});
            skLineSegment(sketch, "E485", {"start": v(62.34, 0) * mm, "end": v(63.84, 0) * mm});
            skLineSegment(sketch, "E486", {"start": v(62.34, -1.5) * mm, "end": v(63.84, -1.5) * mm});
            skLineSegment(sketch, "E487", {"start": v(62.34, -31.75) * mm, "end": v(62.34, -34.75) * mm});
            skLineSegment(sketch, "E488", {"start": v(63.84, -31.75) * mm, "end": v(63.84, -34.75) * mm});
            skLineSegment(sketch, "E489", {"start": v(59.04, -63.5) * mm, "end": v(59.04, -65) * mm});
            skLineSegment(sketch, "E490", {"start": v(60.54, -63.5) * mm, "end": v(60.54, -65) * mm});
            skLineSegment(sketch, "E491.trimOffspring", {"start": v(60.54, -65) * mm, "end": v(62.34, -65) * mm});
            skLineSegment(sketch, "E492", {"start": v(62.34, -65) * mm, "end": v(63.84, -65) * mm});
            skLineSegment(sketch, "E493", {"start": v(63.84, -63.5) * mm, "end": v(62.34, -63.5) * mm});
            skLineSegment(sketch, "E494", {"start": v(65.34, -63.5) * mm, "end": v(65.34, -65) * mm});
            skLineSegment(sketch, "E495", {"start": v(66.84, -63.5) * mm, "end": v(66.84, -65) * mm});
            skLineSegment(sketch, "E496.trimOffspring", {"start": v(66.84, -65) * mm, "end": v(68.34, -65) * mm});
            skLineSegment(sketch, "E497", {"start": v(66.84, -31.75) * mm, "end": v(65.34, -31.75) * mm});
            skLineSegment(sketch, "E498", {"start": v(66.84, -34.75) * mm, "end": v(65.34, -34.75) * mm});
            skLineSegment(sketch, "E499", {"start": v(65.34, -1.5) * mm, "end": v(65.34, 0) * mm});
            skLineSegment(sketch, "E500", {"start": v(66.84, -1.5) * mm, "end": v(66.84, 0) * mm});
            skLineSegment(sketch, "E501.trimOffspring", {"start": v(66.84, 0) * mm, "end": v(68.34, 0) * mm});
            skLineSegment(sketch, "E502.trimOffspring", {"start": v(65.34, -34.75) * mm, "end": v(65.34, -63.5) * mm});
            skLineSegment(sketch, "E503.trimOffspring", {"start": v(66.84, -34.75) * mm, "end": v(66.84, -63.5) * mm});
            skLineSegment(sketch, "E504", {"start": v(68.34, -65) * mm, "end": v(69.84, -65) * mm});
            skLineSegment(sketch, "E505", {"start": v(71.34, -34.75) * mm, "end": v(72.84, -34.75) * mm});
            skLineSegment(sketch, "E506", {"start": v(69.84, -63.5) * mm, "end": v(68.34, -63.5) * mm});
            skLineSegment(sketch, "E507", {"start": v(71.34, -63.5) * mm, "end": v(71.34, -65) * mm});
            skLineSegment(sketch, "E508", {"start": v(72.84, -63.5) * mm, "end": v(72.84, -65) * mm});
            skLineSegment(sketch, "E509.trimOffspring", {"start": v(72.84, -65) * mm, "end": v(74.34, -65) * mm});
            skLineSegment(sketch, "E510.trimOffspring", {"start": v(72.84, -65) * mm, "end": v(77.34, -65) * mm});
            skLineSegment(sketch, "E511", {"start": v(68.34, -31.75) * mm, "end": v(68.34, -34.75) * mm});
            skLineSegment(sketch, "E512", {"start": v(69.84, -34.75) * mm, "end": v(69.84, -31.75) * mm});
            skLineSegment(sketch, "E513", {"start": v(69.84, -1.5) * mm, "end": v(68.34, -1.5) * mm});
            skLineSegment(sketch, "E514", {"start": v(69.84, 0) * mm, "end": v(68.34, 0) * mm});
            skLineSegment(sketch, "E515", {"start": v(71.34, -1.5) * mm, "end": v(71.34, 0) * mm});
            skLineSegment(sketch, "E516", {"start": v(72.84, -1.5) * mm, "end": v(72.84, 0) * mm});
            skLineSegment(sketch, "E517.trimOffspring", {"start": v(72.84, 0) * mm, "end": v(74.34, 0) * mm});
            skLineSegment(sketch, "E518", {"start": v(74.34, 0) * mm, "end": v(77.34, 0) * mm});
            skLineSegment(sketch, "E519.trimOffspring", {"start": v(80.34, -1.5) * mm, "end": v(81.84, -1.5) * mm});
            skLineSegment(sketch, "E520", {"start": v(77.34, -1.5) * mm, "end": v(77.34, 0) * mm});
            skLineSegment(sketch, "E521", {"start": v(78.84, -1.5) * mm, "end": v(78.84, 0) * mm});
            skLineSegment(sketch, "E522", {"start": v(75.84, -1.5) * mm, "end": v(74.34, -1.5) * mm});
            skLineSegment(sketch, "E523", {"start": v(83.34, -1.5) * mm, "end": v(83.34, 0) * mm});
            skLineSegment(sketch, "E524", {"start": v(84.84, -1.5) * mm, "end": v(84.84, 0) * mm});
            skLineSegment(sketch, "E525", {"start": v(89.34, -1.5) * mm, "end": v(89.34, 0) * mm});
            skLineSegment(sketch, "E526", {"start": v(90.84, -1.5) * mm, "end": v(90.84, 0) * mm});
            skLineSegment(sketch, "E527.trimOffspring", {"start": v(78.84, 0) * mm, "end": v(80.34, 0) * mm});
            skLineSegment(sketch, "E528.trimOffspring", {"start": v(78.84, 0) * mm, "end": v(83.34, 0) * mm});
            skLineSegment(sketch, "E529.trimOffspring", {"start": v(84.84, 0) * mm, "end": v(87.84, 0) * mm});
            skLineSegment(sketch, "E530.trimOffspring", {"start": v(84.84, 0) * mm, "end": v(86.34, 0) * mm});
            skLineSegment(sketch, "E531.trimOffspring", {"start": v(90.84, 0) * mm, "end": v(102.34, 0) * mm});
            skLineSegment(sketch, "E532", {"start": v(87.84, -1.5) * mm, "end": v(86.34, -1.5) * mm});
            skLineSegment(sketch, "E533", {"start": v(71.34, -31.75) * mm, "end": v(72.84, -31.75) * mm});
            skLineSegment(sketch, "E534", {"start": v(89.34, -34.75) * mm, "end": v(90.84, -34.75) * mm});
            skLineSegment(sketch, "E535.trimOffspring", {"start": v(71.34, -34.75) * mm, "end": v(71.34, -63.5) * mm});
            skLineSegment(sketch, "E536.trimOffspring", {"start": v(72.84, -34.75) * mm, "end": v(72.84, -63.5) * mm});
            skLineSegment(sketch, "E537.trimOffspring", {"start": v(77.34, -31.75) * mm, "end": v(78.84, -31.75) * mm});
            skLineSegment(sketch, "E538.trimOffspring", {"start": v(77.34, -34.75) * mm, "end": v(78.84, -34.75) * mm});
            skLineSegment(sketch, "E539", {"start": v(74.34, -31.75) * mm, "end": v(74.34, -34.75) * mm});
            skLineSegment(sketch, "E540", {"start": v(75.84, -31.75) * mm, "end": v(75.84, -34.75) * mm});
            skLineSegment(sketch, "E541", {"start": v(80.34, -31.75) * mm, "end": v(80.34, -34.75) * mm});
            skLineSegment(sketch, "E542", {"start": v(81.84, -31.75) * mm, "end": v(81.84, -34.75) * mm});
            skLineSegment(sketch, "E543", {"start": v(86.34, -31.75) * mm, "end": v(86.34, -34.75) * mm});
            skLineSegment(sketch, "E544", {"start": v(87.84, -31.75) * mm, "end": v(87.84, -34.75) * mm});
            skLineSegment(sketch, "E545.trimOffspring", {"start": v(77.34, -34.75) * mm, "end": v(77.34, -63.5) * mm});
            skLineSegment(sketch, "E546.trimOffspring", {"start": v(78.84, -34.75) * mm, "end": v(78.84, -63.5) * mm});
            skLineSegment(sketch, "E547.trimOffspring", {"start": v(83.34, -31.75) * mm, "end": v(84.84, -31.75) * mm});
            skLineSegment(sketch, "E548.trimOffspring", {"start": v(83.34, -34.75) * mm, "end": v(84.84, -34.75) * mm});
            skLineSegment(sketch, "E549.trimOffspring", {"start": v(83.34, -34.75) * mm, "end": v(83.34, -63.5) * mm});
            skLineSegment(sketch, "E550.trimOffspring", {"start": v(84.84, -34.75) * mm, "end": v(84.84, -63.5) * mm});
            skLineSegment(sketch, "E551.trimOffspring", {"start": v(89.34, -31.75) * mm, "end": v(90.84, -31.75) * mm});
            skLineSegment(sketch, "E552.trimOffspring", {"start": v(89.34, -34.75) * mm, "end": v(89.34, -63.5) * mm});
            skLineSegment(sketch, "E553.trimOffspring", {"start": v(90.84, -34.75) * mm, "end": v(90.84, -63.5) * mm});
            skLineSegment(sketch, "E554", {"start": v(74.34, -63.5) * mm, "end": v(75.84, -63.5) * mm});
            skLineSegment(sketch, "E555.trimOffspring", {"start": v(80.34, -63.5) * mm, "end": v(81.84, -63.5) * mm});
            skLineSegment(sketch, "E556", {"start": v(77.34, -63.5) * mm, "end": v(77.34, -65) * mm});
            skLineSegment(sketch, "E557", {"start": v(78.84, -63.5) * mm, "end": v(78.84, -65) * mm});
            skLineSegment(sketch, "E558.trimOffspring", {"start": v(78.84, -65) * mm, "end": v(83.34, -65) * mm});
            skLineSegment(sketch, "E559.trimOffspring", {"start": v(78.84, -65) * mm, "end": v(80.34, -65) * mm});
            skLineSegment(sketch, "E560", {"start": v(83.34, -63.5) * mm, "end": v(83.34, -65) * mm});
            skLineSegment(sketch, "E561", {"start": v(84.84, -63.5) * mm, "end": v(84.84, -65) * mm});
            skLineSegment(sketch, "E562", {"start": v(89.34, -63.5) * mm, "end": v(89.34, -65) * mm});
            skLineSegment(sketch, "E563", {"start": v(90.84, -63.5) * mm, "end": v(90.84, -65) * mm});
            skLineSegment(sketch, "E564.trimOffspring", {"start": v(86.34, -63.5) * mm, "end": v(87.84, -63.5) * mm});
            skLineSegment(sketch, "E565.trimOffspring", {"start": v(84.84, -65) * mm, "end": v(89.34, -65) * mm});
            skLineSegment(sketch, "E566.trimOffspring", {"start": v(84.84, -65) * mm, "end": v(86.34, -65) * mm});
            skLineSegment(sketch, "E567.trimOffspring", {"start": v(90.84, -65) * mm, "end": v(92.34, -65) * mm});
            skLineSegment(sketch, "E568.trimOffspring", {"start": v(90.84, -65) * mm, "end": v(102.34, -65) * mm});
            skSolve(sketch);
        }
        {
            var Q0;
            Q0 = qSketchRegion(id + "F0", true);
            extrude(context, id + "F1", {"entities" : qUnion([Q0]), "depth" : .5 * mm, "offsetDistance" : 25 * mm});
        }
    });
